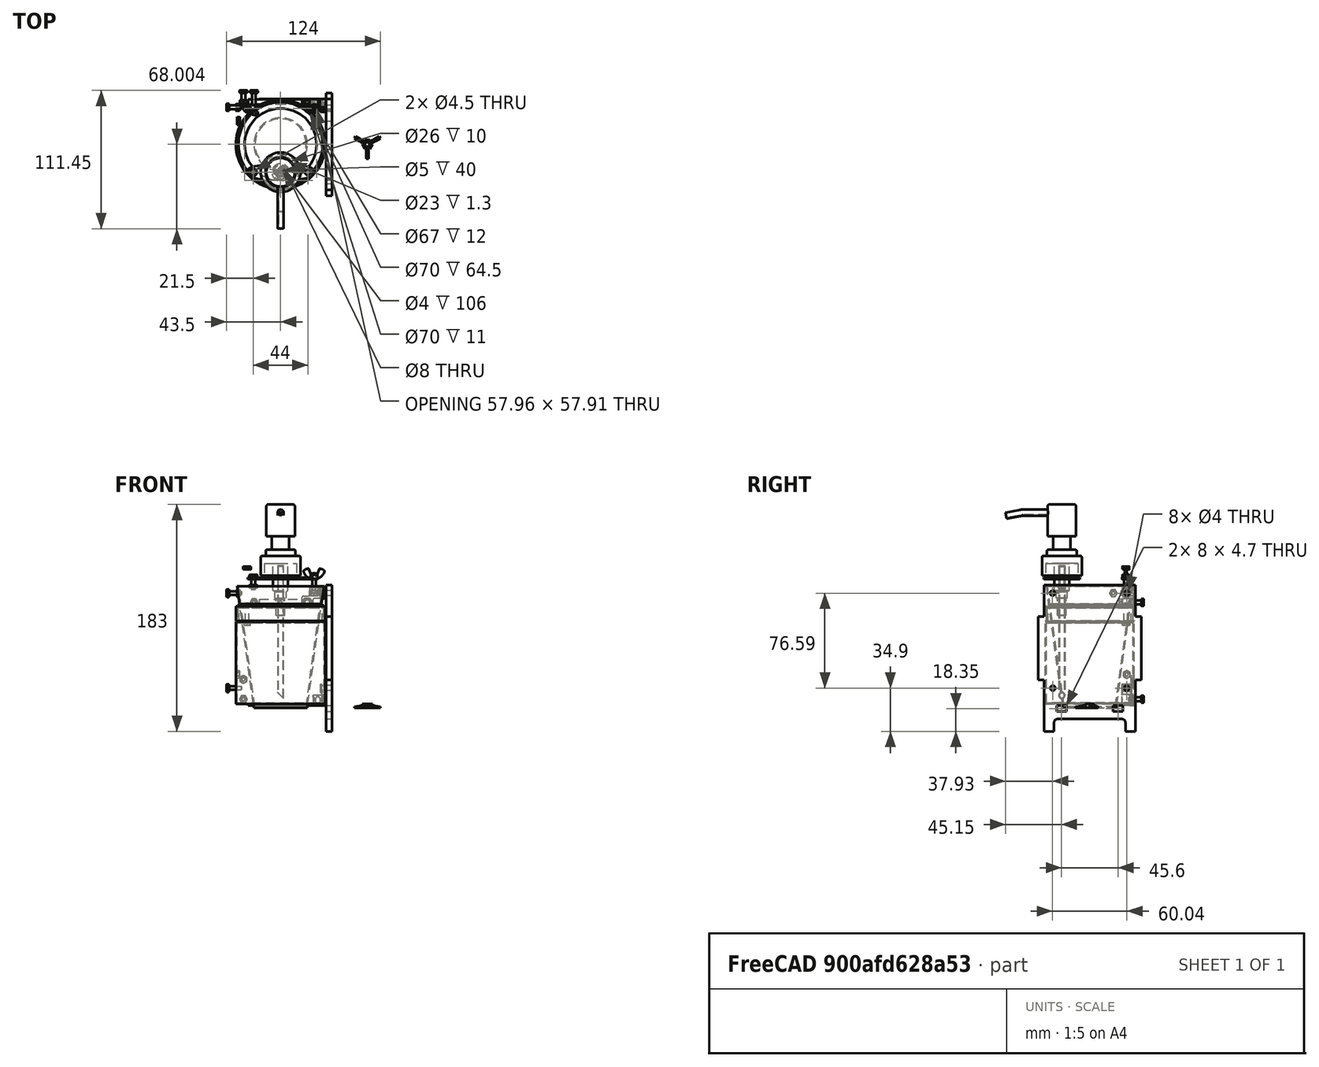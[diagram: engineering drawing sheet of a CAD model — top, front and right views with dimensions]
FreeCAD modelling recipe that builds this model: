
FCSTD DOCUMENT  (FreeCAD 0.20R29410 (Git))
Label: OrcuDispenser_78_realease_1_0
License: All rights reserved
LicenseURL: http://en.wikipedia.org/wiki/All_rights_reserved
objects: Sketcher::SketchObject×45, PartDesign::Body×36, PartDesign::Pad×23, PartDesign::FeatureBase×19, PartDesign::Pocket×16, Part::FeaturePython×14, PartDesign::Fillet×11, App::DocumentObjectGroup×10, Part::Part2DObjectPython×6, PartDesign::Revolution×4, PartDesign::Mirrored×4, Mesh::Feature×4, Part::Mirroring×2, Spreadsheet::Sheet×1, PartDesign::PolarPattern×1, PartDesign::AdditivePipe×1, PartDesign::Chamfer×1
note: 239 computed .brp shape members not serialized (recipe doc carries the construction recipe); baked Part::Feature solids carry a one-line shape summary decoded from their .brp

FEATURE [Sketcher::SketchObject] Sketch006
  FullyConstrained = true
  MapMode = 5
  Placement = pos=(0,0,0) rot=(1,0,0;1.5708rad)
  Support = -> [XZ_Plane004]
  sketch-geometry (6):
    g0: LineSegment StartX=0 StartY=0 StartZ=0 EndX=-21.5 EndY=0 EndZ=0
    g1: LineSegment StartX=-21.5 StartY=0 StartZ=0 EndX=-35 EndY=98 EndZ=0
    g2: LineSegment StartX=-20.6378 StartY=1 StartZ=0 EndX=0 EndY=1 EndZ=0
    g3: LineSegment StartX=0 StartY=1 StartZ=0 EndX=0 EndY=0 EndZ=0
    g4: LineSegment StartX=-20.6378 StartY=1 StartZ=0 EndX=-34 EndY=98 EndZ=0
    g5: LineSegment StartX=-34 StartY=98 StartZ=0 EndX=-35 EndY=98 EndZ=0
  constraints (17):
    c: Coincident(g-1,g0)
    c: PointOnObject(g0,g-1)
    c: Coincident(g0,g1)
    c: PointOnObject(g2,g-2)
    c: Horizontal(g2)
    c: Coincident(g2,g3)
    c: Coincident(g3,g0)
    c: DistanceX(g0,g0) = 21.5
    c: DistanceX(g1,g-1) = 35
    c: DistanceY(g-1,g1) = 98
    c: Coincident(g2,g4)
    c: Coincident(g4,g5)
    c: Coincident(g5,g1)
    c: Horizontal(g5)
    c: Parallel(g4,g1)
    c: DistanceX(g5,g5) = 1
    c: Equal(g3,g5)
FEATURE [PartDesign::Revolution] Revolution002
  Angle = 360
  Axis = (0,-2e-16,1)
  Base = (0,0,0)
  Placement = pos=(0,0,0) rot=(1,0,0;1.5708rad)
  Profile = -> Sketch006
  ReferenceAxis = -> Sketch006 [V_Axis]
FEATURE [PartDesign::Body] Body004  label="Cup (0,2 L)"
  Group = -> [Sketch006,Revolution002]
  Origin = -> Origin004
  Tip = -> Revolution002
FEATURE [Spreadsheet::Sheet] Spreadsheet  label="Parameters"
  cells = A2=Dispenser parameters; A3=123; B3= = Input cells (double-click and modify); A4=123; B4= = Output cells (value ist calculated, do not modify!); A6=Dispenser size; E6=Laser cutting; A7=PlateThickness; B7(PlateThickness)==4.7mm; E7=LCdistance; F7(LCdistance)==4mm; A8=Height; B8(Height)==102mm; A9=Length; B9(Length)==83mm; A10=Width; B10(Width)==83mm; A12=Element dimensions; A13=JointLength; B13(JointLength)==B8 / 2; C13= = Height / 2; A14=Tenon; B14(Tenon)==8mm; A15=LegHeight; B15(LegHeight)==10mm; A16=LegWidth; B16(LegWidth)==8mm; A17=LegRadius; B17(LegRadius)==3mm; A18=TenonDistance; B18(TenonDistance)==10mm; A19=TenonHeight; B19(TenonHeight)==6mm
FEATURE [Sketcher::SketchObject] Sketch012
  FullyConstrained = true
  MapMode = 5
  Support = -> [XY_Plane008]
  expr: Constraints[103] = <<Parameters>>.Width
  expr: Constraints[104] = <<Parameters>>.Length
  expr: Constraints[105] = <<Parameters>>.Width / 2 - <<Parameters>>.PlateThickness - <<Parameters>>.TenonDistance
  expr: Constraints[106] = <<Parameters>>.Length / 2 - <<Parameters>>.PlateThickness - <<Parameters>>.TenonDistance
  expr: Constraints[107] = <<Parameters>>.Width / 2 - <<Parameters>>.PlateThickness - <<Parameters>>.TenonDistance - <<Parameters>>.Tenon
  expr: Constraints[108] = <<Parameters>>.Length / 2 - <<Parameters>>.PlateThickness - <<Parameters>>.TenonDistance - <<Parameters>>.Tenon
  expr: Constraints[88] = <<Parameters>>.Length / 2 - <<Parameters>>.PlateThickness
  expr: Constraints[89] = <<Parameters>>.Width / 2 - <<Parameters>>.PlateThickness
  expr: Constraints[93] = <<Parameters>>.Length / 2 - <<Parameters>>.PlateThickness
  expr: Constraints[94] = <<Parameters>>.Width / 2 - <<Parameters>>.PlateThickness
  sketch-geometry (40):
    g0: LineSegment StartX=-41.5 StartY=41.5 StartZ=0 EndX=41.5 EndY=41.5 EndZ=0
    g1: LineSegment StartX=41.5 StartY=41.5 StartZ=0 EndX=41.5 EndY=-41.5 EndZ=0
    g2: LineSegment StartX=41.5 StartY=-41.5 StartZ=0 EndX=-41.5 EndY=-41.5 EndZ=0
    g3: LineSegment StartX=-41.5 StartY=-41.5 StartZ=0 EndX=-41.5 EndY=41.5 EndZ=0
    g4: LineSegment StartX=-36.8 StartY=-36.8 StartZ=0 EndX=-26.8 EndY=-36.8 EndZ=0
    g5: LineSegment StartX=-26.8 StartY=-36.8 StartZ=0 EndX=-26.8 EndY=-41.5 EndZ=0
    g6: LineSegment StartX=-26.8 StartY=-41.5 StartZ=0 EndX=-18.8 EndY=-41.5 EndZ=0
    g7: LineSegment StartX=-18.8 StartY=-41.5 StartZ=0 EndX=-18.8 EndY=-36.8 EndZ=0
    g8: LineSegment StartX=-18.8 StartY=-36.8 StartZ=0 EndX=18.8 EndY=-36.8 EndZ=0
    g9: LineSegment StartX=18.8 StartY=-36.8 StartZ=0 EndX=18.8 EndY=-41.5 EndZ=0
    g10: LineSegment StartX=18.8 StartY=-41.5 StartZ=0 EndX=26.8 EndY=-41.5 EndZ=0
    g11: LineSegment StartX=26.8 StartY=-41.5 StartZ=0 EndX=26.8 EndY=-36.8 EndZ=0
    g12: LineSegment StartX=26.8 StartY=-36.8 StartZ=0 EndX=36.8 EndY=-36.8 EndZ=0
    g13: LineSegment StartX=36.8 StartY=-36.8 StartZ=0 EndX=36.8 EndY=-26.8 EndZ=0
    g14: LineSegment StartX=36.8 StartY=-26.8 StartZ=0 EndX=41.5 EndY=-26.8 EndZ=0
    g15: LineSegment StartX=41.5 StartY=-26.8 StartZ=0 EndX=41.5 EndY=-18.8 EndZ=0
    g16: LineSegment StartX=41.5 StartY=-18.8 StartZ=0 EndX=36.8 EndY=-18.8 EndZ=0
    g17: LineSegment StartX=36.8 StartY=-18.8 StartZ=0 EndX=36.8 EndY=18.8 EndZ=0
    g18: LineSegment StartX=36.8 StartY=18.8 StartZ=0 EndX=41.5 EndY=18.8 EndZ=0
    g19: LineSegment StartX=41.5 StartY=18.8 StartZ=0 EndX=41.5 EndY=26.8 EndZ=0
    g20: LineSegment StartX=41.5 StartY=26.8 StartZ=0 EndX=36.8 EndY=26.8 EndZ=0
    g21: LineSegment StartX=36.8 StartY=26.8 StartZ=0 EndX=36.8 EndY=36.8 EndZ=0
    g22: LineSegment StartX=36.8 StartY=36.8 StartZ=0 EndX=26.8 EndY=36.8 EndZ=0
    g23: LineSegment StartX=26.8 StartY=36.8 StartZ=0 EndX=26.8 EndY=41.5 EndZ=0
    g24: LineSegment StartX=26.8 StartY=41.5 StartZ=0 EndX=18.8 EndY=41.5 EndZ=0
    g25: LineSegment StartX=18.8 StartY=41.5 StartZ=0 EndX=18.8 EndY=36.8 EndZ=0
    g26: LineSegment StartX=18.8 StartY=36.8 StartZ=0 EndX=-18.8 EndY=36.8 EndZ=0
    g27: LineSegment StartX=-18.8 StartY=36.8 StartZ=0 EndX=-18.8 EndY=41.5 EndZ=0
    g28: LineSegment StartX=-18.8 StartY=41.5 StartZ=0 EndX=-26.8 EndY=41.5 EndZ=0
    g29: LineSegment StartX=-26.8 StartY=41.5 StartZ=0 EndX=-26.8 EndY=36.8 EndZ=0
    g30: LineSegment StartX=-26.8 StartY=36.8 StartZ=0 EndX=-36.8 EndY=36.8 EndZ=0
    g31: LineSegment StartX=-36.8 StartY=36.8 StartZ=0 EndX=-36.8 EndY=26.8 EndZ=0
    g32: LineSegment StartX=-36.8 StartY=26.8 StartZ=0 EndX=-41.5 EndY=26.8 EndZ=0
    g33: LineSegment StartX=-41.5 StartY=26.8 StartZ=0 EndX=-41.5 EndY=18.8 EndZ=0
    g34: LineSegment StartX=-41.5 StartY=18.8 StartZ=0 EndX=-36.8 EndY=18.8 EndZ=0
    g35: LineSegment StartX=-36.8 StartY=18.8 StartZ=0 EndX=-36.8 EndY=-18.8 EndZ=0
    g36: LineSegment StartX=-36.8 StartY=-18.8 StartZ=0 EndX=-41.5 EndY=-18.8 EndZ=0
    g37: LineSegment StartX=-41.5 StartY=-18.8 StartZ=0 EndX=-41.5 EndY=-26.8 EndZ=0
    g38: LineSegment StartX=-41.5 StartY=-26.8 StartZ=0 EndX=-36.8 EndY=-26.8 EndZ=0
    g39: LineSegment StartX=-36.8 StartY=-26.8 StartZ=0 EndX=-36.8 EndY=-36.8 EndZ=0
  constraints (109):
    c: Coincident(g0,g1)
    c: Coincident(g1,g2)
    c: Coincident(g2,g3)
    c: Coincident(g3,g0)
    c: Horizontal(g0)
    c: Vertical(g1)
    c: Horizontal(g4)
    c: Coincident(g4,g5)
    c: PointOnObject(g5,g2)
    c: Vertical(g5)
    c: Coincident(g5,g6)
    c: PointOnObject(g6,g2)
    c: Coincident(g6,g7)
    c: Vertical(g7)
    c: Coincident(g7,g8)
    c: Coincident(g8,g9)
    c: PointOnObject(g9,g2)
    c: Vertical(g9)
    c: Coincident(g9,g10)
    c: PointOnObject(g10,g2)
    c: Coincident(g10,g11)
    c: Vertical(g11)
    c: Coincident(g11,g12)
    c: Horizontal(g12)
    c: Coincident(g12,g13)
    c: Vertical(g13)
    c: Coincident(g13,g14)
    c: PointOnObject(g14,g1)
    c: Coincident(g14,g15)
    c: PointOnObject(g15,g1)
    c: Coincident(g15,g16)
    c: Horizontal(g16)
    c: Coincident(g16,g17)
    c: Vertical(g17)
    c: Coincident(g17,g18)
    c: PointOnObject(g18,g1)
    c: Horizontal(g18)
    c: Coincident(g18,g19)
    c: PointOnObject(g19,g1)
    c: Coincident(g19,g20)
    c: Horizontal(g20)
    c: Coincident(g20,g21)
    c: Vertical(g21)
    c: Coincident(g21,g22)
    c: Horizontal(g22)
    c: Coincident(g22,g23)
    c: PointOnObject(g23,g0)
    c: Vertical(g23)
    c: Coincident(g23,g24)
    c: PointOnObject(g24,g0)
    c: Coincident(g24,g25)
    c: Vertical(g25)
    c: Coincident(g25,g26)
    c: Horizontal(g26)
    c: Coincident(g26,g27)
    c: PointOnObject(g27,g0)
    c: Vertical(g27)
    c: Coincident(g27,g28)
    c: PointOnObject(g28,g0)
    c: Coincident(g28,g29)
    c: Vertical(g29)
    c: Coincident(g29,g30)
    c: Coincident(g30,g31)
    c: Vertical(g31)
    c: Coincident(g31,g32)
    c: PointOnObject(g32,g3)
    c: Horizontal(g32)
    c: Coincident(g32,g33)
    c: PointOnObject(g33,g3)
    c: Coincident(g33,g34)
    c: Horizontal(g34)
    c: Coincident(g34,g35)
    c: Coincident(g35,g36)
    c: Horizontal(g36)
    c: Coincident(g36,g37)
    c: PointOnObject(g37,g3)
    c: Coincident(g37,g38)
    c: Horizontal(g38)
    c: Coincident(g38,g39)
    c: Coincident(g39,g4)
    c: Vertical(g39)
    c: Horizontal(g14)
    c: Equal(g10,g6)
    c: Equal(g37,g33)
    c: Equal(g28,g24)
    c: Equal(g24,g19)
    c: Symmetric(g1,g2,g-2)
    c: Symmetric(g2,g0,g-1)
    c: DistanceY(g7,g-1) = 36.8
    c: DistanceX(g38,g-1) = 36.8
    c: Symmetric(g29,g4,g-1)
    c: Symmetric(g7,g26,g-1)
    c: Symmetric(g11,g22,g-1)
    c: DistanceY(g4,g-1) = 36.8
    c: DistanceX(g35,g-1) = 36.8
    c: Symmetric(g36,g33,g-1)
    c: Symmetric(g38,g13,g-2)
    c: Symmetric(g35,g16,g-2)
    c: Symmetric(g31,g20,g-2)
    c: Symmetric(g4,g30,g-1)
    c: Vertical(g35)
    c: Horizontal(g8)
    c: Symmetric(g11,g4,g-2)
    c: DistanceX(g2,g2) = 83
    c: DistanceY(g3,g3) = 83
    c: DistanceX(g4,g-1) = 26.8
    c: DistanceY(g38,g-1) = 26.8
    c: DistanceX(g6,g-1) = 18.8
    c: DistanceY(g36,g-1) = 18.8
FEATURE [PartDesign::Pad] Pad008
  AlongSketchNormal = false
  Direction = (0,0,1)
  Length = 4.7
  Length2 = 100
  Profile = -> Sketch012
  Reversed = true
  Type = 0
  expr: Length = <<Parameters>>.PlateThickness
FEATURE [PartDesign::Body] Body008  label="Bottom"
  Group = -> [Sketch012,Pad008]
  Origin = -> Origin008
  Placement = pos=(0,0,1.7) rot=(0,0,1;0rad)
  Tip = -> Pad008
  expr: .Placement.Base.z = <<Parameters>>.PlateThickness - 3mm - (<<Parameters>>.Height - 102mm) / 2
FEATURE [Sketcher::SketchObject] Sketch013
  FullyConstrained = true
  MapMode = 5
  Placement = pos=(0,0,0) rot=(1,0,0;1.5708rad)
  Support = -> [XZ_Plane009]
  expr: Constraints[32] = <<Parameters>>.JointLength
  expr: Constraints[35] = <<Parameters>>.PlateThickness
  expr: Constraints[50] = <<Parameters>>.LegWidth
  expr: Constraints[51] = <<Parameters>>.LegHeight
  expr: Constraints[53] = <<Parameters>>.LegHeight + <<Parameters>>.TenonHeight
  expr: Constraints[62] = <<Parameters>>.Tenon
  expr: Constraints[63] = <<Parameters>>.PlateThickness
  expr: Constraints[64] = <<Parameters>>.TenonDistance + <<Parameters>>.PlateThickness
  expr: Constraints[8] = <<Parameters>>.Width
  expr: Constraints[9] = <<Parameters>>.Height
  sketch-geometry (30):
    g0: LineSegment StartX=-41.5 StartY=51 StartZ=0 EndX=41.5 EndY=51 EndZ=0
    g1: LineSegment StartX=41.5 StartY=51 StartZ=0 EndX=41.5 EndY=-51 EndZ=0
    g2: LineSegment StartX=41.5 StartY=-51 StartZ=0 EndX=-41.5 EndY=-51 EndZ=0
    g3: LineSegment StartX=-41.5 StartY=-51 StartZ=0 EndX=-41.5 EndY=51 EndZ=0
    g4: LineSegment StartX=-41.5 StartY=-51 StartZ=0 EndX=-41.5 EndY=-25.5 EndZ=0
    g5: LineSegment StartX=-41.5 StartY=-25.5 StartZ=0 EndX=-36.8 EndY=-25.5 EndZ=0
    g6: LineSegment StartX=-36.8 StartY=-25.5 StartZ=0 EndX=-36.8 EndY=25.5 EndZ=0
    g7: LineSegment StartX=-36.8 StartY=25.5 StartZ=0 EndX=-41.5 EndY=25.5 EndZ=0
    g8: LineSegment StartX=-41.5 StartY=25.5 StartZ=0 EndX=-41.5 EndY=51 EndZ=0
    g9: LineSegment StartX=-41.5 StartY=51 StartZ=0 EndX=41.5 EndY=51 EndZ=0
    g10: LineSegment StartX=41.5 StartY=51 StartZ=0 EndX=41.5 EndY=25.5 EndZ=0
    g11: LineSegment StartX=41.5 StartY=25.5 StartZ=0 EndX=36.8 EndY=25.5 EndZ=0
    g12: LineSegment StartX=36.8 StartY=25.5 StartZ=0 EndX=36.8 EndY=-25.5 EndZ=0
    g13: LineSegment StartX=36.8 StartY=-25.5 StartZ=0 EndX=41.5 EndY=-25.5 EndZ=0
    g14: LineSegment StartX=41.5 StartY=-25.5 StartZ=0 EndX=41.5 EndY=-51 EndZ=0
    g15: LineSegment StartX=-41.5 StartY=-51 StartZ=0 EndX=-41.5 EndY=-67 EndZ=0
    g16: LineSegment StartX=-41.5 StartY=-67 StartZ=0 EndX=-33.5 EndY=-67 EndZ=0
    g17: LineSegment StartX=-33.5 StartY=-67 StartZ=0 EndX=-33.5 EndY=-57 EndZ=0
    g18: LineSegment StartX=-33.5 StartY=-57 StartZ=0 EndX=33.5 EndY=-57 EndZ=0
    g19: LineSegment StartX=33.5 StartY=-57 StartZ=0 EndX=33.5 EndY=-67 EndZ=0
    g20: LineSegment StartX=33.5 StartY=-67 StartZ=0 EndX=41.5 EndY=-67 EndZ=0
    g21: LineSegment StartX=41.5 StartY=-67 StartZ=0 EndX=41.5 EndY=-51 EndZ=0
    g22: LineSegment StartX=-26.8 StartY=-46.3 StartZ=0 EndX=-18.8 EndY=-46.3 EndZ=0
    g23: LineSegment StartX=-18.8 StartY=-46.3 StartZ=0 EndX=-18.8 EndY=-51 EndZ=0
    g24: LineSegment StartX=-18.8 StartY=-51 StartZ=0 EndX=-26.8 EndY=-51 EndZ=0
    g25: LineSegment StartX=-26.8 StartY=-51 StartZ=0 EndX=-26.8 EndY=-46.3 EndZ=0
    g26: LineSegment StartX=18.8 StartY=-46.3 StartZ=0 EndX=26.8 EndY=-46.3 EndZ=0
    g27: LineSegment StartX=26.8 StartY=-46.3 StartZ=0 EndX=26.8 EndY=-51 EndZ=0
    g28: LineSegment StartX=26.8 StartY=-51 StartZ=0 EndX=18.8 EndY=-51 EndZ=0
    g29: LineSegment StartX=18.8 StartY=-51 StartZ=0 EndX=18.8 EndY=-46.3 EndZ=0
  constraints (78):
    c: Coincident(g0,g1)
    c: Coincident(g1,g2)
    c: Coincident(g2,g3)
    c: Coincident(g3,g0)
    c: Horizontal(g0)
    c: Vertical(g1)
    c: Symmetric(g2,g1,g-2)
    c: Symmetric(g2,g0,g-1)
    c: DistanceX(g2,g2) = 83
    c: DistanceY(g3,g3) = 102
    c: Coincident(g2,g4)
    c: PointOnObject(g4,g3)
    c: Coincident(g4,g5)
    c: Horizontal(g5)
    c: Coincident(g5,g6)
    c: Vertical(g6)
    c: Coincident(g6,g7)
    c: Horizontal(g7)
    c: Coincident(g7,g8)
    c: Coincident(g8,g0)
    c: Coincident(g8,g9)
    c: Coincident(g9,g0)
    c: Coincident(g9,g10)
    c: PointOnObject(g10,g1)
    c: Coincident(g10,g11)
    c: Horizontal(g11)
    c: Coincident(g11,g12)
    c: Vertical(g12)
    c: Coincident(g12,g13)
    c: Horizontal(g13)
    c: Coincident(g13,g14)
    c: Coincident(g14,g1)
    c: DistanceY(g6,g6) = 51
    c: Symmetric(g7,g4,g-1)
    c: Symmetric(g10,g13,g-1)
    c: DistanceX(g7,g7) = 4.7
    c: Coincident(g4,g15)
    c: Vertical(g15)
    c: Coincident(g15,g16)
    c: Horizontal(g16)
    c: Coincident(g16,g17)
    c: Vertical(g17)
    c: Coincident(g17,g18)
    c: Coincident(g18,g19)
    c: Vertical(g19)
    c: Coincident(g19,g20)
    c: Horizontal(g20)
    c: Coincident(g20,g21)
    c: Coincident(g21,g14)
    c: Vertical(g21)
    c: DistanceX(g16,g16) = 8
    c: DistanceY(g17,g17) = 10
    c: Equal(g19,g17)
    c: DistanceY(g15,g15) = 16
    c: Coincident(g22,g23)
    c: Coincident(g23,g24)
    c: Coincident(g24,g25)
    c: Coincident(g25,g22)
    c: Horizontal(g22)
    c: Horizontal(g24)
    c: Vertical(g23)
    c: Vertical(g25)
    c: DistanceX(g24,g24) = 8
    c: DistanceY(g25,g25) = 4.7
    c: DistanceX(g4,g24) = 14.7
    c: PointOnObject(g24,g2)
    c: Coincident(g26,g27)
    c: Coincident(g27,g28)
    c: Coincident(g28,g29)
    c: Coincident(g29,g26)
    c: Horizontal(g26)
    c: Horizontal(g28)
    c: Vertical(g27)
    c: Vertical(g29)
    c: Symmetric(g28,g23,g-2)
    c: Symmetric(g26,g22,g-2)
    c: Symmetric(g18,g17,g-2)
    c: Symmetric(g11,g6,g-2)
FEATURE [PartDesign::Pad] Pad009
  AlongSketchNormal = false
  Direction = (0,-1,-2e-16)
  Length = 4.7
  Length2 = 100
  Placement = pos=(0,0,0) rot=(1,0,0;1.5708rad)
  Profile = -> Sketch013
  Type = 0
  expr: Length = <<Parameters>>.PlateThickness
FEATURE [Sketcher::SketchObject] Sketch014
  FullyConstrained = true
  MapMode = 5
  Placement = pos=(0,0,0) rot=(1,0,0;1.5708rad)
  Support = -> [XZ_Plane010]
  expr: Constraints[32] = <<Parameters>>.JointLength
  expr: Constraints[35] = <<Parameters>>.PlateThickness
  expr: Constraints[50] = <<Parameters>>.LegWidth
  expr: Constraints[51] = <<Parameters>>.LegHeight
  expr: Constraints[53] = <<Parameters>>.LegHeight + <<Parameters>>.TenonHeight
  expr: Constraints[62] = <<Parameters>>.Tenon
  expr: Constraints[63] = <<Parameters>>.PlateThickness
  expr: Constraints[64] = <<Parameters>>.TenonDistance + <<Parameters>>.PlateThickness
  expr: Constraints[8] = <<Parameters>>.Width
  expr: Constraints[9] = <<Parameters>>.Height
  sketch-geometry (30):
    g0: LineSegment StartX=-41.5 StartY=51 StartZ=0 EndX=41.5 EndY=51 EndZ=0
    g1: LineSegment StartX=41.5 StartY=51 StartZ=0 EndX=41.5 EndY=-51 EndZ=0
    g2: LineSegment StartX=41.5 StartY=-51 StartZ=0 EndX=-41.5 EndY=-51 EndZ=0
    g3: LineSegment StartX=-41.5 StartY=-51 StartZ=0 EndX=-41.5 EndY=51 EndZ=0
    g4: LineSegment StartX=-41.5 StartY=-51 StartZ=0 EndX=-41.5 EndY=-25.5 EndZ=0
    g5: LineSegment StartX=-41.5 StartY=-25.5 StartZ=0 EndX=-36.8 EndY=-25.5 EndZ=0
    g6: LineSegment StartX=-36.8 StartY=-25.5 StartZ=0 EndX=-36.8 EndY=25.5 EndZ=0
    g7: LineSegment StartX=-36.8 StartY=25.5 StartZ=0 EndX=-41.5 EndY=25.5 EndZ=0
    g8: LineSegment StartX=-41.5 StartY=25.5 StartZ=0 EndX=-41.5 EndY=51 EndZ=0
    g9: LineSegment StartX=-41.5 StartY=51 StartZ=0 EndX=41.5 EndY=51 EndZ=0
    g10: LineSegment StartX=41.5 StartY=51 StartZ=0 EndX=41.5 EndY=25.5 EndZ=0
    g11: LineSegment StartX=41.5 StartY=25.5 StartZ=0 EndX=36.8 EndY=25.5 EndZ=0
    g12: LineSegment StartX=36.8 StartY=25.5 StartZ=0 EndX=36.8 EndY=-25.5 EndZ=0
    g13: LineSegment StartX=36.8 StartY=-25.5 StartZ=0 EndX=41.5 EndY=-25.5 EndZ=0
    g14: LineSegment StartX=41.5 StartY=-25.5 StartZ=0 EndX=41.5 EndY=-51 EndZ=0
    g15: LineSegment StartX=-41.5 StartY=-51 StartZ=0 EndX=-41.5 EndY=-67 EndZ=0
    g16: LineSegment StartX=-41.5 StartY=-67 StartZ=0 EndX=-33.5 EndY=-67 EndZ=0
    g17: LineSegment StartX=-33.5 StartY=-67 StartZ=0 EndX=-33.5 EndY=-57 EndZ=0
    g18: LineSegment StartX=-33.5 StartY=-57 StartZ=0 EndX=33.5 EndY=-57 EndZ=0
    g19: LineSegment StartX=33.5 StartY=-57 StartZ=0 EndX=33.5 EndY=-67 EndZ=0
    g20: LineSegment StartX=33.5 StartY=-67 StartZ=0 EndX=41.5 EndY=-67 EndZ=0
    g21: LineSegment StartX=41.5 StartY=-67 StartZ=0 EndX=41.5 EndY=-51 EndZ=0
    g22: LineSegment StartX=-26.8 StartY=-46.3 StartZ=0 EndX=-18.8 EndY=-46.3 EndZ=0
    g23: LineSegment StartX=-18.8 StartY=-46.3 StartZ=0 EndX=-18.8 EndY=-51 EndZ=0
    g24: LineSegment StartX=-18.8 StartY=-51 StartZ=0 EndX=-26.8 EndY=-51 EndZ=0
    g25: LineSegment StartX=-26.8 StartY=-51 StartZ=0 EndX=-26.8 EndY=-46.3 EndZ=0
    g26: LineSegment StartX=18.8 StartY=-46.3 StartZ=0 EndX=26.8 EndY=-46.3 EndZ=0
    g27: LineSegment StartX=26.8 StartY=-46.3 StartZ=0 EndX=26.8 EndY=-51 EndZ=0
    g28: LineSegment StartX=26.8 StartY=-51 StartZ=0 EndX=18.8 EndY=-51 EndZ=0
    g29: LineSegment StartX=18.8 StartY=-51 StartZ=0 EndX=18.8 EndY=-46.3 EndZ=0
  constraints (78):
    c: Coincident(g0,g1)
    c: Coincident(g1,g2)
    c: Coincident(g2,g3)
    c: Coincident(g3,g0)
    c: Horizontal(g0)
    c: Vertical(g1)
    c: Symmetric(g2,g1,g-2)
    c: Symmetric(g2,g0,g-1)
    c: DistanceX(g2,g2) = 83
    c: DistanceY(g3,g3) = 102
    c: Coincident(g2,g4)
    c: PointOnObject(g4,g3)
    c: Coincident(g4,g5)
    c: Horizontal(g5)
    c: Coincident(g5,g6)
    c: Vertical(g6)
    c: Coincident(g6,g7)
    c: Horizontal(g7)
    c: Coincident(g7,g8)
    c: Coincident(g8,g0)
    c: Coincident(g8,g9)
    c: Coincident(g9,g0)
    c: Coincident(g9,g10)
    c: PointOnObject(g10,g1)
    c: Coincident(g10,g11)
    c: Horizontal(g11)
    c: Coincident(g11,g12)
    c: Vertical(g12)
    c: Coincident(g12,g13)
    c: Horizontal(g13)
    c: Coincident(g13,g14)
    c: Coincident(g14,g1)
    c: DistanceY(g6,g6) = 51
    c: Symmetric(g7,g4,g-1)
    c: Symmetric(g10,g13,g-1)
    c: DistanceX(g7,g7) = 4.7
    c: Coincident(g4,g15)
    c: Vertical(g15)
    c: Coincident(g15,g16)
    c: Horizontal(g16)
    c: Coincident(g16,g17)
    c: Vertical(g17)
    c: Coincident(g17,g18)
    c: Coincident(g18,g19)
    c: Vertical(g19)
    c: Coincident(g19,g20)
    c: Horizontal(g20)
    c: Coincident(g20,g21)
    c: Coincident(g21,g14)
    c: Vertical(g21)
    c: DistanceX(g16,g16) = 8
    c: DistanceY(g17,g17) = 10
    c: Equal(g19,g17)
    c: DistanceY(g15,g15) = 16
    c: Coincident(g22,g23)
    c: Coincident(g23,g24)
    c: Coincident(g24,g25)
    c: Coincident(g25,g22)
    c: Horizontal(g22)
    c: Horizontal(g24)
    c: Vertical(g23)
    c: Vertical(g25)
    c: DistanceX(g24,g24) = 8
    c: DistanceY(g25,g25) = 4.7
    c: DistanceX(g4,g24) = 14.7
    c: PointOnObject(g24,g2)
    c: Coincident(g26,g27)
    c: Coincident(g27,g28)
    c: Coincident(g28,g29)
    c: Coincident(g29,g26)
    c: Horizontal(g26)
    c: Horizontal(g28)
    c: Vertical(g27)
    c: Vertical(g29)
    c: Symmetric(g28,g23,g-2)
    c: Symmetric(g26,g22,g-2)
    c: Symmetric(g18,g17,g-2)
    c: Symmetric(g11,g6,g-2)
FEATURE [PartDesign::Pad] Pad010
  AlongSketchNormal = false
  Direction = (0,-1,-2e-16)
  Length = 4.7
  Length2 = 100
  Placement = pos=(0,0,0) rot=(1,0,0;1.5708rad)
  Profile = -> Sketch014
  ReferenceAxis = -> Sketch014 [N_Axis]
  Type = 0
  expr: Length = <<Parameters>>.PlateThickness
FEATURE [Sketcher::SketchObject] Sketch015
  FullyConstrained = true
  MapMode = 5
  Placement = pos=(0,0,0) rot=(1,0,0;1.5708rad)
  Support = -> [XZ_Plane011]
  expr: Constraints[10] = <<Parameters>>.JointLength
  expr: Constraints[16] = <<Parameters>>.LegHeight
  expr: Constraints[26] = <<Parameters>>.Tenon
  expr: Constraints[27] = <<Parameters>>.PlateThickness
  expr: Constraints[28] = <<Parameters>>.TenonDistance + <<Parameters>>.PlateThickness
  expr: Constraints[73] = <<Parameters>>.PlateThickness
  expr: Constraints[75] = <<Parameters>>.LegWidth
  expr: Constraints[76] = <<Parameters>>.LegHeight + <<Parameters>>.TenonHeight
  expr: Constraints[8] = <<Parameters>>.Length
  expr: Constraints[9] = <<Parameters>>.Height
  sketch-geometry (30):
    g0: LineSegment StartX=-41.5 StartY=51 StartZ=0 EndX=41.5 EndY=51 EndZ=0
    g1: LineSegment StartX=41.5 StartY=51 StartZ=0 EndX=41.5 EndY=-51 EndZ=0
    g2: LineSegment StartX=41.5 StartY=-51 StartZ=0 EndX=-41.5 EndY=-51 EndZ=0
    g3: LineSegment StartX=-41.5 StartY=-51 StartZ=0 EndX=-41.5 EndY=51 EndZ=0
    g4: LineSegment StartX=-41.5 StartY=-25.5 StartZ=0 EndX=-41.5 EndY=25.5 EndZ=0
    g5: LineSegment StartX=41.5 StartY=25.5 StartZ=0 EndX=41.5 EndY=-25.5 EndZ=0
    g6: LineSegment StartX=-28.8 StartY=-67 StartZ=0 EndX=-28.8 EndY=-57 EndZ=0
    g7: LineSegment StartX=-28.8 StartY=-57 StartZ=0 EndX=28.8 EndY=-57 EndZ=0
    g8: LineSegment StartX=28.8 StartY=-57 StartZ=0 EndX=28.8 EndY=-67 EndZ=0
    g9: LineSegment StartX=-26.8 StartY=-46.3 StartZ=0 EndX=-18.8 EndY=-46.3 EndZ=0
    g10: LineSegment StartX=-18.8 StartY=-46.3 StartZ=0 EndX=-18.8 EndY=-51 EndZ=0
    g11: LineSegment StartX=-18.8 StartY=-51 StartZ=0 EndX=-26.8 EndY=-51 EndZ=0
    g12: LineSegment StartX=-26.8 StartY=-51 StartZ=0 EndX=-26.8 EndY=-46.3 EndZ=0
    g13: LineSegment StartX=18.8 StartY=-46.3 StartZ=0 EndX=26.8 EndY=-46.3 EndZ=0
    g14: LineSegment StartX=26.8 StartY=-46.3 StartZ=0 EndX=26.8 EndY=-51 EndZ=0
    g15: LineSegment StartX=26.8 StartY=-51 StartZ=0 EndX=18.8 EndY=-51 EndZ=0
    g16: LineSegment StartX=18.8 StartY=-51 StartZ=0 EndX=18.8 EndY=-46.3 EndZ=0
    g17: LineSegment StartX=-41.5 StartY=-25.5 StartZ=0 EndX=-36.8 EndY=-25.5 EndZ=0
    g18: LineSegment StartX=-36.8 StartY=-67 StartZ=0 EndX=-28.8 EndY=-67 EndZ=0
    g19: LineSegment StartX=28.8 StartY=-67 StartZ=0 EndX=36.8 EndY=-67 EndZ=0
    g20: LineSegment StartX=-36.8 StartY=-25.5 StartZ=0 EndX=-36.8 EndY=-51 EndZ=0
    g21: LineSegment StartX=-36.8 StartY=-51 StartZ=0 EndX=-36.8 EndY=-67 EndZ=0
    g22: LineSegment StartX=36.8 StartY=-67 StartZ=0 EndX=36.8 EndY=-51 EndZ=0
    g23: LineSegment StartX=36.8 StartY=-51 StartZ=0 EndX=36.8 EndY=-25.5 EndZ=0
    g24: LineSegment StartX=36.8 StartY=-25.5 StartZ=0 EndX=41.5 EndY=-25.5 EndZ=0
    g25: LineSegment StartX=-41.5 StartY=25.5 StartZ=0 EndX=-36.8 EndY=25.5 EndZ=0
    g26: LineSegment StartX=-36.8 StartY=25.5 StartZ=0 EndX=-36.8 EndY=51 EndZ=0
    g27: LineSegment StartX=-36.8 StartY=51 StartZ=0 EndX=36.8 EndY=51 EndZ=0
    g28: LineSegment StartX=36.8 StartY=51 StartZ=0 EndX=36.8 EndY=25.5 EndZ=0
    g29: LineSegment StartX=36.8 StartY=25.5 StartZ=0 EndX=41.5 EndY=25.5 EndZ=0
  constraints (81):
    c: Coincident(g0,g1)
    c: Coincident(g1,g2)
    c: Coincident(g2,g3)
    c: Coincident(g3,g0)
    c: Horizontal(g0)
    c: Vertical(g1)
    c: Symmetric(g2,g1,g-2)
    c: Symmetric(g2,g0,g-1)
    c: DistanceX(g2,g2) = 83
    c: DistanceY(g3,g3) = 102
    c: DistanceY(g4,g4) = 51
    c: Equal(g5,g4)
    c: Vertical(g6)
    c: Coincident(g6,g7)
    c: Coincident(g7,g8)
    c: Vertical(g8)
    c: DistanceY(g6,g6) = 10
    c: Equal(g8,g6)
    c: Coincident(g9,g10)
    c: Coincident(g10,g11)
    c: Coincident(g11,g12)
    c: Coincident(g12,g9)
    c: Horizontal(g9)
    c: Horizontal(g11)
    c: Vertical(g10)
    c: Vertical(g12)
    c: DistanceX(g11,g11) = 8
    c: DistanceY(g12,g12) = 4.7
    c: DistanceX(g2,g11) = 14.7
    c: PointOnObject(g11,g2)
    c: Coincident(g13,g14)
    c: Coincident(g14,g15)
    c: Coincident(g15,g16)
    c: Coincident(g16,g13)
    c: Horizontal(g13)
    c: Horizontal(g15)
    c: Vertical(g14)
    c: Vertical(g16)
    c: Symmetric(g15,g10,g-2)
    c: Symmetric(g4,g4,g-1)
    c: PointOnObject(g4,g3)
    c: PointOnObject(g5,g1)
    c: Symmetric(g5,g5,g-1)
    c: Coincident(g4,g17)
    c: Horizontal(g17)
    c: Coincident(g18,g6)
    c: Horizontal(g18)
    c: Coincident(g8,g19)
    c: Horizontal(g19)
    c: Coincident(g17,g20)
    c: PointOnObject(g20,g2)
    c: Vertical(g20)
    c: Coincident(g20,g21)
    c: Coincident(g21,g18)
    c: Vertical(g21)
    c: Coincident(g19,g22)
    c: PointOnObject(g22,g2)
    c: Vertical(g22)
    c: Coincident(g22,g23)
    c: Vertical(g23)
    c: Coincident(g23,g24)
    c: Coincident(g24,g5)
    c: Coincident(g4,g25)
    c: Horizontal(g25)
    c: Coincident(g25,g26)
    c: PointOnObject(g26,g0)
    c: Vertical(g26)
    c: Coincident(g26,g27)
    c: PointOnObject(g27,g0)
    c: Coincident(g27,g28)
    c: Vertical(g28)
    c: Coincident(g28,g29)
    c: Coincident(g29,g5)
    c: DistanceX(g25,g25) = 4.7
    c: Equal(g17,g25)
    c: DistanceX(g18,g18) = 8
    c: DistanceY(g21,g21) = 16
    c: Symmetric(g9,g13,g-2)
    c: Symmetric(g7,g6,g-2)
    c: Symmetric(g28,g25,g-2)
    c: Symmetric(g17,g23,g-2)
FEATURE [PartDesign::Pad] Pad011
  AlongSketchNormal = false
  Direction = (0,-1,-2e-16)
  Length = 4.7
  Length2 = 100
  Placement = pos=(0,0,0) rot=(1,0,0;1.5708rad)
  Profile = -> Sketch015
  ReferenceAxis = -> Sketch015 [N_Axis]
  Type = 0
  expr: Length = <<Parameters>>.PlateThickness
FEATURE [Sketcher::SketchObject] Sketch016
  FullyConstrained = true
  MapMode = 5
  Support = -> [XY_Plane013]
  expr: Constraints[8] = <<Parameters>>.Width + 6mm
  expr: Constraints[9] = <<Parameters>>.Length + 6mm
  sketch-geometry (9):
    g0: LineSegment StartX=-44.5 StartY=44.5 StartZ=0 EndX=44.5 EndY=44.5 EndZ=0
    g1: LineSegment StartX=44.5 StartY=44.5 StartZ=0 EndX=44.5 EndY=-44.5 EndZ=0
    g2: LineSegment StartX=44.5 StartY=-44.5 StartZ=0 EndX=-44.5 EndY=-44.5 EndZ=0
    g3: LineSegment StartX=-44.5 StartY=-44.5 StartZ=0 EndX=-44.5 EndY=44.5 EndZ=0
    g4: Circle CenterX=0 CenterY=-22.5 CenterZ=0 NormalX=0 NormalY=0 NormalZ=1 AngleXU=0 Radius=8.5
    g5: LineSegment StartX=0 StartY=-22.5 StartZ=0 EndX=-22 EndY=-22.5 EndZ=0
    g6: LineSegment StartX=0 StartY=-22.5 StartZ=0 EndX=22 EndY=-22.5 EndZ=0
    g7: Circle CenterX=-22 CenterY=-22.5 CenterZ=0 NormalX=0 NormalY=0 NormalZ=1 AngleXU=0 Radius=2
    g8: Circle CenterX=22 CenterY=-22.5 CenterZ=0 NormalX=0 NormalY=0 NormalZ=1 AngleXU=0 Radius=2
  constraints (23):
    c: Coincident(g0,g1)
    c: Coincident(g1,g2)
    c: Coincident(g2,g3)
    c: Coincident(g3,g0)
    c: Horizontal(g0)
    c: Vertical(g1)
    c: Symmetric(g2,g1,g-2)
    c: Symmetric(g2,g0,g-1)
    c: DistanceX(g2,g2) = 89
    c: DistanceY(g3,g3) = 89
    c: PointOnObject(g4,g-2)
    c: Diameter(g4) = 17
    c: DistanceY(g1,g4) = 22
    c: Coincident(g5,g4)
    c: Horizontal(g5)
    c: Coincident(g6,g4)
    c: Horizontal(g6)
    c: Equal(g6,g5)
    c: Coincident(g7,g5)
    c: Diameter(g7) = 4
    c: Coincident(g8,g6)
    c: Equal(g8,g7)
    c: DistanceX(g6,g6) = 22
FEATURE [PartDesign::Pad] Pad012
  AlongSketchNormal = false
  Direction = (0,0,1)
  Length = 4.7
  Length2 = 100
  Profile = -> Sketch016
  Type = 0
  expr: Length = <<Parameters>>.PlateThickness
FEATURE [PartDesign::Fillet] Fillet002
  Base = -> Pad009 [Edge44,Edge41]
  BaseFeature = -> Pad009
  Placement = pos=(0,0,0) rot=(1,0,0;1.5708rad)
  Radius = 3
  SupportTransform = false
  UseAllEdges = false
FEATURE [PartDesign::Fillet] Fillet003
  Base = -> Pad010 [Edge44,Edge41]
  BaseFeature = -> Pad010
  Placement = pos=(0,0,0) rot=(1,0,0;1.5708rad)
  Radius = 3
  SupportTransform = false
  UseAllEdges = false
FEATURE [PartDesign::Fillet] Fillet004
  Base = -> Pad011 [Edge38,Edge41]
  BaseFeature = -> Pad011
  Placement = pos=(0,0,0) rot=(1,0,0;1.5708rad)
  Radius = 3
  SupportTransform = false
  UseAllEdges = false
FEATURE [PartDesign::FeatureBase] Clone001
  BaseFeature = -> Body008
FEATURE [PartDesign::Body] Body014  label="LC_Bottom"
  BaseFeature = -> Body008
  Group = -> [Clone001]
  Origin = -> Origin014
  Placement = pos=(535,-80.5,0) rot=(0,0,1;0rad)
  Tip = -> Clone001
  expr: .Placement.Base.x = <<Parameters>>.Width + 100mm + <<Parameters>>.Width + 5 * <<Parameters>>.LCdistance + <<Parameters>>.Length + <<Parameters>>.Width + <<Parameters>>.Length
  expr: .Placement.Base.y = -(<<Parameters>>.Length + <<Parameters>>.LCdistance - 6.5mm)
FEATURE [Part::Part2DObjectPython] Shape2DView  label="Shape_Bottom"  # Draft 2D object (typed FeaturePython)
  AutoUpdate = true
  Base = -> Body014
  Clip = false
  FuseArch = false
  HiddenLines = false
  InPlace = true
  OnlySolids = false
  Projection = (0,0,1)
  ProjectionMode = 0
  SegmentLength = 0.05
  Tessellation = false
  VisibleOnly = false
FEATURE [Sketcher::SketchObject] Sketch017
  FullyConstrained = true
  MapMode = 5
  Placement = pos=(0,0,0) rot=(1,0,0;1.5708rad)
  Support = -> [XZ_Plane020]
  sketch-geometry (10):
    g0: LineSegment StartX=0 StartY=0 StartZ=0 EndX=-36 EndY=0 EndZ=0
    g1: LineSegment StartX=-36 StartY=0 StartZ=0 EndX=-36 EndY=66.5 EndZ=0
    g2: LineSegment StartX=-35 StartY=1 StartZ=0 EndX=0 EndY=1 EndZ=0
    g3: LineSegment StartX=0 StartY=1 StartZ=0 EndX=0 EndY=0 EndZ=0
    g4: LineSegment StartX=-35 StartY=1 StartZ=0 EndX=-35 EndY=65.5 EndZ=0
    g5: LineSegment StartX=-35 StartY=65.5 StartZ=0 EndX=-33.5 EndY=65.5 EndZ=0
    g6: LineSegment StartX=-33.5 StartY=65.5 StartZ=0 EndX=-33.5 EndY=77.5 EndZ=0
    g7: LineSegment StartX=-33.5 StartY=77.5 StartZ=0 EndX=-34.5 EndY=77.5 EndZ=0
    g8: LineSegment StartX=-34.5 StartY=77.5 StartZ=0 EndX=-34.5 EndY=66.5 EndZ=0
    g9: LineSegment StartX=-34.5 StartY=66.5 StartZ=0 EndX=-36 EndY=66.5 EndZ=0
  constraints (29):
    c: Coincident(g-1,g0)
    c: PointOnObject(g0,g-1)
    c: Coincident(g0,g1)
    c: PointOnObject(g2,g-2)
    c: Horizontal(g2)
    c: Coincident(g2,g3)
    c: Coincident(g3,g0)
    c: DistanceX(g0,g0) = 36
    c: DistanceY(g-1,g1) = 66.5
    c: Coincident(g2,g4)
    c: Parallel(g4,g1)
    c: DistanceX(g1,g4) = 1
    c: Vertical(g1)
    c: Coincident(g4,g5)
    c: Horizontal(g5)
    c: Coincident(g5,g6)
    c: Vertical(g6)
    c: Coincident(g6,g7)
    c: Horizontal(g7)
    c: Coincident(g7,g8)
    c: Vertical(g8)
    c: Coincident(g8,g9)
    c: Horizontal(g9)
    c: DistanceY(g6,g6) = 12
    c: DistanceY(g5,g8) = 1
    c: DistanceX(g7,g7) = 1
    c: Coincident(g9,g1)
    c: DistanceX(g9,g9) = 1.5
    c: DistanceY(g3,g3) = 1
FEATURE [PartDesign::Revolution] Revolution004
  Angle = 360
  Axis = (0,-2e-16,1)
  Base = (0,0,0)
  Placement = pos=(0,0,0) rot=(1,0,0;1.5708rad)
  Profile = -> Sketch017
  ReferenceAxis = -> Sketch017 [V_Axis]
FEATURE [PartDesign::Body] Body020  label="Jar (0,2 L)"
  Group = -> [Sketch017,Revolution004]
  Origin = -> Origin020
  Placement = pos=(0,0,3) rot=(0,0,1;0rad)
  Tip = -> Revolution004
FEATURE [Sketcher::SketchObject] Sketch018
  ExternalGeometry = -> [Fillet004]
  FullyConstrained = true
  MapMode = 5
  Placement = pos=(0,0,0) rot=(-1,0,0;1.5708rad)
  Support = -> [Fillet004]
  sketch-geometry (4):
    g0: Circle CenterX=30.02 CenterY=-44.49 CenterZ=0 NormalX=0 NormalY=0 NormalZ=1 AngleXU=0 Radius=2
    g1: Circle CenterX=-30.02 CenterY=-44.49 CenterZ=0 NormalX=0 NormalY=0 NormalZ=1 AngleXU=0 Radius=2
    g2: Circle CenterX=29.8 CenterY=32.1 CenterZ=0 NormalX=0 NormalY=0 NormalZ=1 AngleXU=0 Radius=2
    g3: Circle CenterX=-29.8 CenterY=32.1 CenterZ=0 NormalX=0 NormalY=0 NormalZ=1 AngleXU=0 Radius=2
  constraints (10):
    c: Diameter(g0) = 4
    c: DistanceY(g-3,g0) = 6.51
    c: DistanceX(g0,g-3) = 6.78
    c: Equal(g1,g0)
    c: DistanceX(g-4,g2) = 3
    c: DistanceY(g2,g-4) = 14.2
    c: Equal(g2,g0)
    c: Equal(g3,g2)
    c: Symmetric(g3,g2,g-2)
    c: Symmetric(g1,g0,g-2)
FEATURE [PartDesign::Pocket] Pocket
  BaseFeature = -> Fillet004
  Direction = (0,-1,-2e-16)
  Length = 5
  Length2 = 5
  Placement = pos=(0,0,0) rot=(1,0,0;1.5708rad)
  Profile = -> Sketch018
  ReferenceAxis = -> Sketch018 [N_Axis]
  Type = 1
FEATURE [PartDesign::Body] Body011  label="Side_Left"
  Group = -> [Sketch015,Pad011,Fillet004,Sketch018,Pocket]
  Origin = -> Origin011
  Placement = pos=(-41.5,0,48) rot=(0,0,1;1.5708rad)
  Tip = -> Pocket
  expr: .Placement.Base.x = -(<<Parameters>>.Width / 2)
FEATURE [PartDesign::FeatureBase] Clone
  BaseFeature = -> Body011
  Placement = pos=(-39,-3.5e-14,48) rot=(0,0,1;1.5708rad)
FEATURE [PartDesign::Body] Body012  label="Side_Right (clone)"
  BaseFeature = -> Body011
  Group = -> [Clone]
  Origin = -> Origin012
  Placement = pos=(75.8,0,0) rot=(0,0,1;0rad)
  Tip = -> Clone
  expr: .Placement.Base.x = <<Parameters>>.Width / 2 + 39mm - <<Parameters>>.PlateThickness
FEATURE [PartDesign::FeatureBase] Clone004
  BaseFeature = -> Body011
FEATURE [PartDesign::Body] Body017  label="LC_Side_Left"
  BaseFeature = -> Body011
  Group = -> [Clone004]
  Origin = -> Origin017
  Placement = pos=(270,0,0) rot=(0,0.707107,0.707107;3.14159rad)
  Tip = -> Clone004
  expr: .Placement.Base.x = <<Parameters>>.Width + 100mm + <<Parameters>>.Width + <<Parameters>>.LCdistance
FEATURE [PartDesign::FeatureBase] Clone005
  BaseFeature = -> Body017
FEATURE [PartDesign::Body] Body018  label="LC_Side_Right"
  BaseFeature = -> Body017
  Group = -> [Clone005]
  Origin = -> Origin018
  Placement = pos=(444,0,0) rot=(-1,0,0;1.5708rad)
  Tip = -> Clone005
  expr: .Placement.Base.x = <<Parameters>>.Width + 100mm + <<Parameters>>.Width + 3 * <<Parameters>>.LCdistance + <<Parameters>>.Length + <<Parameters>>.Width
FEATURE [Part::Part2DObjectPython] Shape2DView003  label="Shape_Side_Left"  # Draft 2D object (typed FeaturePython)
  AutoUpdate = true
  Base = -> Body017
  Clip = false
  FuseArch = false
  HiddenLines = false
  InPlace = true
  OnlySolids = false
  Projection = (0,0,1)
  ProjectionMode = 0
  SegmentLength = 0.05
  Tessellation = false
  VisibleOnly = false
FEATURE [Part::Part2DObjectPython] Shape2DView004  label="Shape_Side_Right"  # Draft 2D object (typed FeaturePython)
  AutoUpdate = true
  Base = -> Body018
  Clip = false
  FuseArch = false
  HiddenLines = false
  InPlace = true
  OnlySolids = false
  Projection = (0,0,1)
  ProjectionMode = 0
  SegmentLength = 0.05
  Tessellation = false
  VisibleOnly = false
FEATURE [Sketcher::SketchObject] Sketch019
  ExternalGeometry = -> [Fillet003]
  FullyConstrained = true
  MapMode = 5
  Placement = pos=(0,0,0) rot=(-1,0,0;1.5708rad)
  Support = -> [Fillet003]
  sketch-geometry (2):
    g0: Circle CenterX=-21.5 CenterY=-37 CenterZ=0 NormalX=0 NormalY=0 NormalZ=1 AngleXU=0 Radius=2
    g1: Circle CenterX=-30 CenterY=41.1 CenterZ=0 NormalX=0 NormalY=0 NormalZ=1 AngleXU=0 Radius=2
  constraints (6):
    c: Diameter(g0) = 4
    c: DistanceY(g-3,g0) = 14
    c: DistanceX(g-3,g0) = 20
    c: Equal(g1,g0)
    c: DistanceX(g1,g-4) = 3.2
    c: DistanceY(g1,g-4) = 5.2
FEATURE [PartDesign::Pocket] Pocket001
  BaseFeature = -> Fillet003
  Direction = (0,-1,-2e-16)
  Length = 5
  Length2 = 5
  Placement = pos=(0,0,0) rot=(1,0,0;1.5708rad)
  Profile = -> Sketch019
  ReferenceAxis = -> Sketch019 [N_Axis]
  Type = 1
FEATURE [PartDesign::Mirrored] Mirrored
  BaseFeature = -> Pocket001
  MirrorPlane = -> Sketch019 [V_Axis]
  Originals = -> [Pocket001]
  Placement = pos=(0,0,0) rot=(1,0,0;1.5708rad)
FEATURE [PartDesign::Body] Body010  label="Back"
  Group = -> [Sketch014,Pad010,Fillet003,Sketch019,Pocket001,Mirrored]
  Origin = -> Origin010
  Placement = pos=(0,41.5,48) rot=(0,0,1;0rad)
  Tip = -> Mirrored
  expr: .Placement.Base.y = <<Parameters>>.Length / 2
FEATURE [PartDesign::FeatureBase] Clone003
  BaseFeature = -> Body010
FEATURE [PartDesign::Body] Body016  label="LC_Back"
  BaseFeature = -> Body010
  Group = -> [Clone003]
  Origin = -> Origin016
  Placement = pos=(357,0,0) rot=(0,0.707107,0.707107;3.14159rad)
  Tip = -> Clone003
  expr: .Placement.Base.x = <<Parameters>>.Width + 100mm + <<Parameters>>.Width + 2 * <<Parameters>>.LCdistance + <<Parameters>>.Length
FEATURE [Part::Part2DObjectPython] Shape2DView002  label="Shape_Back"  # Draft 2D object (typed FeaturePython)
  AutoUpdate = true
  Base = -> Body016
  Clip = false
  FuseArch = false
  HiddenLines = false
  InPlace = true
  OnlySolids = false
  Projection = (0,0,1)
  ProjectionMode = 0
  SegmentLength = 0.05
  Tessellation = false
  VisibleOnly = false
FEATURE [Sketcher::SketchObject] Sketch020
  ExternalGeometry = -> [Fillet002]
  FullyConstrained = true
  MapMode = 5
  Placement = pos=(0,-4.7,0) rot=(1,0,0;1.5708rad)
  Support = -> [Fillet002]
  sketch-geometry (2):
    g0: Circle CenterX=-21.5 CenterY=37 CenterZ=0 NormalX=0 NormalY=0 NormalZ=1 AngleXU=0 Radius=2
    g1: Circle CenterX=-30 CenterY=-41.1 CenterZ=0 NormalX=0 NormalY=0 NormalZ=1 AngleXU=0 Radius=2
  constraints (6):
    c: Diameter(g0) = 4
    c: DistanceY(g0,g-3) = 14
    c: DistanceX(g-3,g0) = 20
    c: DistanceX(g1,g-4) = 3.2
    c: DistanceY(g-4,g1) = 5.2
    c: Equal(g1,g0)
FEATURE [PartDesign::Pocket] Pocket002
  BaseFeature = -> Fillet002
  Direction = (0,1,-2e-16)
  Length = 5
  Length2 = 5
  Placement = pos=(0,0,0) rot=(1,0,0;1.5708rad)
  Profile = -> Sketch020
  ReferenceAxis = -> Sketch020 [N_Axis]
  Type = 1
FEATURE [PartDesign::Mirrored] Mirrored001
  BaseFeature = -> Pocket002
  MirrorPlane = -> Sketch020 [V_Axis]
  Originals = -> [Pocket002]
  Placement = pos=(0,0,0) rot=(1,0,0;1.5708rad)
FEATURE [PartDesign::Body] Body009  label="Front"
  Group = -> [Sketch013,Pad009,Fillet002,Sketch020,Pocket002,Mirrored001]
  Origin = -> Origin009
  Placement = pos=(0,-36.8,48) rot=(0,0,1;0rad)
  Tip = -> Mirrored001
  expr: .Placement.Base.y = -(<<Parameters>>.Length / 2 - <<Parameters>>.PlateThickness)
FEATURE [PartDesign::FeatureBase] Clone002
  BaseFeature = -> Body009
FEATURE [PartDesign::Body] Body015  label="LC_Front"
  BaseFeature = -> Body009
  Group = -> [Clone002]
  Origin = -> Origin015
  Placement = pos=(183,0,0) rot=(-1,0,0;1.5708rad)
  Tip = -> Clone002
  expr: .Placement.Base.x = <<Parameters>>.Width + 100mm
FEATURE [Part::Part2DObjectPython] Shape2DView001  label="Shape_Front"  # Draft 2D object (typed FeaturePython)
  AutoUpdate = true
  Base = -> Body015
  Clip = false
  FuseArch = false
  HiddenLines = false
  InPlace = true
  OnlySolids = false
  Projection = (0,0,1)
  ProjectionMode = 0
  SegmentLength = 0.05
  Tessellation = false
  VisibleOnly = false
FEATURE [Sketcher::SketchObject] Sketch021
  ExternalGeometry = -> [Pad012]
  FullyConstrained = true
  MapMode = 5
  Placement = pos=(0,0,4.7) rot=(0,0,1;0rad)
  Support = -> [Pad012]
  sketch-geometry (1):
    g0: Circle CenterX=-27 CenterY=29.1 CenterZ=0 NormalX=0 NormalY=0 NormalZ=1 AngleXU=0 Radius=2
  constraints (3):
    c: Diameter(g0) = 4
    c: DistanceX(g-3,g0) = 17.5
    c: DistanceY(g0,g-3) = 15.4
FEATURE [PartDesign::Pocket] Pocket003
  BaseFeature = -> Pad012
  Direction = (0,0,-1)
  Length = 5
  Length2 = 5
  Profile = -> Sketch021
  ReferenceAxis = -> Sketch021 [N_Axis]
  Type = 1
FEATURE [PartDesign::Mirrored] Mirrored002
  BaseFeature = -> Pocket003
  MirrorPlane = -> Sketch021 [V_Axis]
  Originals = -> [Pocket003]
FEATURE [PartDesign::Body] Body013  label="Lid"
  Group = -> [Sketch016,Pad012,Sketch021,Pocket003,Mirrored002]
  Origin = -> Origin013
  Placement = pos=(0,0,99) rot=(0,0,1;0rad)
  Tip = -> Mirrored002
  expr: .Placement.Base.z = 99mm + (<<Parameters>>.Height - 102mm) / 2
FEATURE [PartDesign::FeatureBase] Clone006
  BaseFeature = -> Body013
FEATURE [PartDesign::Body] Body019  label="LC_Lid"
  BaseFeature = -> Body013
  Group = -> [Clone006]
  Origin = -> Origin019
  Placement = pos=(535,6.5,0) rot=(0,0,1;0rad)
  Tip = -> Clone006
  expr: .Placement.Base.x = <<Parameters>>.Width + 100mm + <<Parameters>>.Width + 5 * <<Parameters>>.LCdistance + <<Parameters>>.Length + <<Parameters>>.Width + <<Parameters>>.Length
FEATURE [App::DocumentObjectGroup] Group002  label="Lasercut parts"
  Group = -> [Body008,Body009,Body010,Body011,Body012,Body013]
FEATURE [App::DocumentObjectGroup] Group003  label="Lasercut parts (clones)"
  Group = -> [Body015,Body017,Body016,Body018,Body019,Body014]
FEATURE [Part::Part2DObjectPython] Shape2DView005  label="Shape_Lid"  # Draft 2D object (typed FeaturePython)
  AutoUpdate = true
  Base = -> Body019
  Clip = false
  FuseArch = false
  HiddenLines = false
  InPlace = true
  OnlySolids = false
  Projection = (0,0,1)
  ProjectionMode = 0
  SegmentLength = 0.05
  Tessellation = false
  VisibleOnly = false
FEATURE [App::DocumentObjectGroup] Group004  label="Projections for Lasercutting"
  Group = -> [Shape2DView001,Shape2DView003,Shape2DView002,Shape2DView004,Shape2DView005,Shape2DView,Group003]
FEATURE [Sketcher::SketchObject] Sketch037
  FullyConstrained = true
  MapMode = 5
  Placement = pos=(0,0,0) rot=(1,0,0;1.5708rad)
  Support = -> [XZ_Plane024]
  sketch-geometry (26):
    g0: Circle CenterX=0 CenterY=0 CenterZ=0 NormalX=0 NormalY=0 NormalZ=1 AngleXU=0 Radius=2
    g1: LineSegment StartX=4.5 StartY=-4 StartZ=0 EndX=-4.3 EndY=-4 EndZ=0
    g2: LineSegment StartX=-14.8 StartY=11.74 StartZ=0 EndX=-9.8 EndY=11.74 EndZ=0
    g3: LineSegment StartX=-9.8 StartY=11.74 StartZ=0 EndX=-9.8 EndY=9.5 EndZ=0
    g4: LineSegment StartX=-9.8 StartY=9.5 StartZ=0 EndX=2.5 EndY=9.5 EndZ=0
    g5: LineSegment StartX=2.5 StartY=9.5 StartZ=0 EndX=2.5 EndY=5 EndZ=0
    g6: LineSegment StartX=2.5 StartY=5 StartZ=0 EndX=4.5 EndY=5 EndZ=0
    g7: LineSegment StartX=4.5 StartY=5 StartZ=0 EndX=4.5 EndY=-4 EndZ=0
    g8: LineSegment StartX=-14.8 StartY=3.24 StartZ=0 EndX=-14.8 EndY=7.49 EndZ=0
    g9: LineSegment StartX=-14.8 StartY=11.74 StartZ=0 EndX=-14.8 EndY=7.49 EndZ=0
    g10: LineSegment StartX=-14.8 StartY=3.24 StartZ=0 EndX=-4.3 EndY=3.24 EndZ=0
    g11: LineSegment StartX=-4.3 StartY=3.24 StartZ=0 EndX=-4.3 EndY=-4 EndZ=0
    g12: LineSegment StartX=-3.2909 StartY=0 StartZ=0 EndX=-1.64545 EndY=-2.85 EndZ=0
    g13: LineSegment StartX=-1.64545 StartY=-2.85 StartZ=0 EndX=1.64545 EndY=-2.85 EndZ=0
    g14: LineSegment StartX=1.64545 StartY=-2.85 StartZ=0 EndX=3.2909 EndY=4e-16 EndZ=0
    g15: LineSegment StartX=3.2909 StartY=4e-16 StartZ=0 EndX=1.64545 EndY=2.85 EndZ=0
    g16: LineSegment StartX=1.64545 StartY=2.85 StartZ=0 EndX=-1.64545 EndY=2.85 EndZ=0
    g17: LineSegment StartX=-1.64545 StartY=2.85 StartZ=0 EndX=-3.2909 EndY=0 EndZ=0
    g18: Circle CenterX=0 CenterY=0 CenterZ=0 NormalX=0 NormalY=0 NormalZ=1 AngleXU=0 Radius=3.2909
    g19: LineSegment StartX=-4.0909 StartY=-4e-16 StartZ=0 EndX=-2.04545 EndY=-3.54282 EndZ=0
    g20: LineSegment StartX=-2.04545 StartY=-3.54282 StartZ=0 EndX=2.04545 EndY=-3.54282 EndZ=0
    g21: LineSegment StartX=2.04545 StartY=-3.54282 StartZ=0 EndX=4.0909 EndY=0 EndZ=0
    g22: LineSegment StartX=4.0909 StartY=0 StartZ=0 EndX=2.04545 EndY=3.54282 EndZ=0
    g23: LineSegment StartX=2.04545 StartY=3.54282 StartZ=0 EndX=-2.04545 EndY=3.54282 EndZ=0
    g24: LineSegment StartX=-2.04545 StartY=3.54282 StartZ=0 EndX=-4.0909 EndY=-4e-16 EndZ=0
    g25: Circle CenterX=0 CenterY=0 CenterZ=0 NormalX=0 NormalY=0 NormalZ=1 AngleXU=0 Radius=4.0909
  constraints (67):
    c: Coincident(g0,g-1)
    c: Diameter(g0) = 4
    c: Horizontal(g1)
    c: Horizontal(g2)
    c: Coincident(g2,g3)
    c: Vertical(g3)
    c: Coincident(g3,g4)
    c: Horizontal(g4)
    c: Coincident(g4,g5)
    c: Vertical(g5)
    c: Coincident(g5,g6)
    c: Horizontal(g6)
    c: Coincident(g6,g7)
    c: Coincident(g7,g1)
    c: Vertical(g7)
    c: Vertical(g8)
    c: Coincident(g9,g2)
    c: Coincident(g9,g8)
    c: Vertical(g9)
    c: Equal(g8,g9)
    c: DistanceY(g8,g8) = 4.25
    c: DistanceY(g1,g-1) = 4
    c: DistanceX(g-1,g1) = 4.5
    c: DistanceY(g1,g8) = 7.24
    c: DistanceY(g7,g7) = 9
    c: DistanceX(g6,g6) = 2
    c: DistanceY(g5,g5) = 4.5
    c: DistanceX(g2,g2) = 5
    c: DistanceX(g4,g4) = 12.3
    c: Coincident(g8,g10)
    c: Horizontal(g10)
    c: Coincident(g10,g11)
    c: Coincident(g11,g1)
    c: Vertical(g11)
    c: Coincident(g12,g13)
    c: Coincident(g13,g14)
    c: Coincident(g14,g15)
    c: Coincident(g15,g16)
    c: Coincident(g16,g17)
    c: Coincident(g17,g12)
    c: Equal(g12, g13-g17) x5
    c: PointOnObject(g12,g18)
    c: PointOnObject(g13,g18)
    c: PointOnObject(g14,g18)
    c: PointOnObject(g15,g18)
    c: PointOnObject(g16,g18)
    c: PointOnObject(g17,g18)
    c: Coincident(g18,g0)
    c: PointOnObject(g17,g-1)
    c: DistanceY(g12,g16) = 5.7
    c: Coincident(g19,g20)
    c: Coincident(g20,g21)
    c: Coincident(g21,g22)
    c: Coincident(g22,g23)
    c: Coincident(g23,g24)
    c: Coincident(g24,g19)
    c: Equal(g19, g20-g24) x5
    c: PointOnObject(g19,g25)
    c: PointOnObject(g20,g25)
    c: PointOnObject(g21,g25)
    c: PointOnObject(g22,g25)
    c: PointOnObject(g23,g25)
    c: PointOnObject(g24,g25)
    c: Coincident(g25,g0)
    c: PointOnObject(g24,g-1)
    c: DistanceX(g19,g12) = 0.8
    c: DistanceX(g10,g10) = 10.5
FEATURE [PartDesign::Pad] Pad022
  Direction = (0,-1,-2e-16)
  Length = 1.3
  Length2 = 10
  Placement = pos=(0,0,0) rot=(1,0,0;1.5708rad)
  Profile = -> Sketch037
  ReferenceAxis = -> Sketch037 [N_Axis]
  Type = 0
FEATURE [Sketcher::SketchObject] Sketch038
  FullyConstrained = true
  MapMode = 5
  Placement = pos=(0,-1.3,0) rot=(1,0,0;1.5708rad)
  Support = -> [Pad022]
  sketch-geometry (14):
    g0: LineSegment StartX=-3.2909 StartY=0 StartZ=0 EndX=-1.64545 EndY=-2.85 EndZ=0
    g1: LineSegment StartX=-1.64545 StartY=-2.85 StartZ=0 EndX=1.64545 EndY=-2.85 EndZ=0
    g2: LineSegment StartX=1.64545 StartY=-2.85 StartZ=0 EndX=3.2909 EndY=0 EndZ=0
    g3: LineSegment StartX=3.2909 StartY=0 StartZ=0 EndX=1.64545 EndY=2.85 EndZ=0
    g4: LineSegment StartX=1.64545 StartY=2.85 StartZ=0 EndX=-1.64545 EndY=2.85 EndZ=0
    g5: LineSegment StartX=-1.64545 StartY=2.85 StartZ=0 EndX=-3.2909 EndY=0 EndZ=0
    g6: Circle CenterX=0 CenterY=0 CenterZ=0 NormalX=0 NormalY=0 NormalZ=1 AngleXU=0 Radius=3.2909
    g7: LineSegment StartX=-4.0909 StartY=0 StartZ=0 EndX=-2.04545 EndY=-3.54282 EndZ=0
    g8: LineSegment StartX=-2.04545 StartY=-3.54282 StartZ=0 EndX=2.04545 EndY=-3.54282 EndZ=0
    g9: LineSegment StartX=2.04545 StartY=-3.54282 StartZ=0 EndX=4.0909 EndY=5.032e-13 EndZ=0
    g10: LineSegment StartX=4.0909 StartY=5.032e-13 StartZ=0 EndX=2.04545 EndY=3.54282 EndZ=0
    g11: LineSegment StartX=2.04545 StartY=3.54282 StartZ=0 EndX=-2.04545 EndY=3.54282 EndZ=0
    g12: LineSegment StartX=-2.04545 StartY=3.54282 StartZ=0 EndX=-4.0909 EndY=0 EndZ=0
    g13: Circle CenterX=0 CenterY=0 CenterZ=0 NormalX=0 NormalY=0 NormalZ=1 AngleXU=0 Radius=4.0909
  constraints (32):
    c: Coincident(g0,g1)
    c: Coincident(g1,g2)
    c: Coincident(g2,g3)
    c: Coincident(g3,g4)
    c: Coincident(g4,g5)
    c: Coincident(g5,g0)
    c: Equal(g0, g1-g5) x5
    c: PointOnObject(g0,g6)
    c: PointOnObject(g1,g6)
    c: PointOnObject(g2,g6)
    c: PointOnObject(g3,g6)
    c: PointOnObject(g4,g6)
    c: PointOnObject(g5,g6)
    c: Coincident(g6,g-1)
    c: PointOnObject(g5,g-1)
    c: DistanceY(g0,g4) = 5.7
    c: Coincident(g7,g8)
    c: Coincident(g8,g9)
    c: Coincident(g9,g10)
    c: Coincident(g10,g11)
    c: Coincident(g11,g12)
    c: Coincident(g12,g7)
    c: Equal(g7, g8-g12) x5
    c: PointOnObject(g7,g13)
    c: PointOnObject(g8,g13)
    c: PointOnObject(g9,g13)
    c: PointOnObject(g10,g13)
    c: PointOnObject(g11,g13)
    c: PointOnObject(g12,g13)
    c: Coincident(g13,g6)
    c: PointOnObject(g12,g-1)
    c: DistanceX(g7,g0) = 0.8
FEATURE [PartDesign::Pad] Pad023
  BaseFeature = -> Pad022
  Direction = (0,-1,-2e-16)
  Length = 2.7
  Length2 = 10
  Placement = pos=(0,0,0) rot=(1,0,0;1.5708rad)
  Profile = -> Sketch038
  ReferenceAxis = -> Sketch038 [N_Axis]
  Type = 0
FEATURE [Sketcher::SketchObject] Sketch039
  ExternalGeometry = -> [Pad023]
  FullyConstrained = false
  MapMode = 5
  Placement = pos=(0,-1.3,0) rot=(1,0,0;1.5708rad)
  Support = -> [Pad023]
  sketch-geometry (8):
    g0: LineSegment StartX=-2 StartY=9.5 StartZ=0 EndX=-9 EndY=9.5 EndZ=0
    g1: LineSegment StartX=-9 StartY=9.5 StartZ=0 EndX=-9 EndY=7.5 EndZ=0
    g2: LineSegment StartX=-9 StartY=7.5 StartZ=0 EndX=-2 EndY=7.5 EndZ=0
    g3: LineSegment StartX=-2 StartY=7.5 StartZ=0 EndX=-2 EndY=9.5 EndZ=0
    g4: LineSegment StartX=-9 StartY=8.7441 StartZ=0 EndX=-7 EndY=8.7441 EndZ=0
    g5: LineSegment StartX=-7 StartY=8.7441 StartZ=0 EndX=-5.5 EndY=8.7441 EndZ=0
    g6: LineSegment StartX=-5.5 StartY=8.7441 StartZ=0 EndX=-4 EndY=8.7441 EndZ=0
    g7: LineSegment StartX=-4 StartY=8.7441 StartZ=0 EndX=-2 EndY=8.7441 EndZ=0
  constraints (24):
    c: Coincident(g0,g1)
    c: Coincident(g1,g2)
    c: Coincident(g2,g3)
    c: Coincident(g3,g0)
    c: Horizontal(g0)
    c: Horizontal(g2)
    c: Vertical(g1)
    c: Vertical(g3)
    c: PointOnObject(g0,g-3)
    c: PointOnObject(g4,g1)
    c: Horizontal(g4)
    c: Coincident(g4,g5)
    c: Horizontal(g5)
    c: Coincident(g5,g6)
    c: Horizontal(g6)
    c: Coincident(g6,g7)
    c: PointOnObject(g7,g3)
    c: Horizontal(g7)
    c: Equal(g5,g6)
    c: Equal(g4,g7)
    c: DistanceX(g5,g5) = 1.5
    c: DistanceX(g0,g0) = 7
    c: DistanceX(g0,g-3) = 4.5
    c: DistanceY(g3,g3) = 2
FEATURE [PartDesign::Pad] Pad024
  BaseFeature = -> Pad023
  Direction = (0,-1,-2e-16)
  Length = 10
  Length2 = 10
  Placement = pos=(0,0,0) rot=(1,0,0;1.5708rad)
  Profile = -> Sketch039
  ReferenceAxis = -> Sketch039 [N_Axis]
  Type = 0
FEATURE [Sketcher::SketchObject] Sketch040
  FullyConstrained = true
  MapMode = 5
  Placement = pos=(0,2.1e-15,9.5) rot=(0,0,1;3.14159rad)
  Support = -> [Pad024]
  sketch-geometry (1):
    g0: Circle CenterX=5.5 CenterY=7.7 CenterZ=0 NormalX=0 NormalY=0 NormalZ=1 AngleXU=0 Radius=2
  constraints (3):
    c: Diameter(g0) = 4
    c: DistanceY(g-1,g0) = 7.7
    c: DistanceX(g-1,g0) = 5.5
FEATURE [PartDesign::Pocket] Pocket010
  BaseFeature = -> Pad024
  Direction = (0,2e-16,-1)
  Length = 2
  Length2 = 5
  Placement = pos=(0,0,0) rot=(1,0,0;1.5708rad)
  Profile = -> Sketch040
  ReferenceAxis = -> Sketch040 [N_Axis]
  Type = 0
FEATURE [Sketcher::SketchObject] Sketch041
  ExternalGeometry = -> [Pocket010]
  FullyConstrained = true
  MapMode = 5
  Placement = pos=(-14.8,0,0) rot=(0.707107,0,-0.707107;3.14159rad)
  Support = -> [Pocket010]
  sketch-geometry (6):
    g0: LineSegment StartX=-11.74 StartY=1.3 StartZ=0 EndX=-3.24 EndY=1.3 EndZ=0
    g1: LineSegment StartX=-3.24 StartY=1.3 StartZ=0 EndX=-3.24 EndY=10.2 EndZ=0
    g2: LineSegment StartX=-3.24 StartY=10.2 StartZ=0 EndX=-11.74 EndY=10.2 EndZ=0
    g3: LineSegment StartX=-11.74 StartY=10.2 StartZ=0 EndX=-11.74 EndY=1.3 EndZ=0
    g4: LineSegment StartX=-7.49 StartY=1.3 StartZ=0 EndX=-7.49 EndY=10.2 EndZ=0
    g5: Circle CenterX=-7.49 CenterY=6.8 CenterZ=0 NormalX=0 NormalY=0 NormalZ=1 AngleXU=0 Radius=2
  constraints (16):
    c: Coincident(g0,g1)
    c: Coincident(g1,g2)
    c: Coincident(g2,g3)
    c: Coincident(g3,g0)
    c: Horizontal(g2)
    c: Vertical(g1)
    c: Vertical(g3)
    c: Coincident(g0,g-3)
    c: Coincident(g0,g-4)
    c: Coincident(g4,g-4)
    c: PointOnObject(g4,g2)
    c: Vertical(g4)
    c: PointOnObject(g5,g4)
    c: Diameter(g5) = 4
    c: DistanceY(g-1,g5) = 6.8
    c: DistanceY(g5,g1) = 3.4
FEATURE [PartDesign::Pad] Pad025
  BaseFeature = -> Pocket010
  Direction = (-1,0,-2e-16)
  Length = 5
  Length2 = 10
  Placement = pos=(0,0,0) rot=(1,0,0;1.5708rad)
  Profile = -> Sketch041
  ReferenceAxis = -> Sketch041 [N_Axis]
  Reversed = true
  Type = 0
FEATURE [Sketcher::SketchObject] Sketch042
  ExternalGeometry = -> [Pad025]
  FullyConstrained = true
  MapMode = 5
  Placement = pos=(-14.8,1e-16,-3e-15) rot=(0.707107,0,-0.707107;3.14159rad)
  Support = -> [Pad025]
  sketch-geometry (16):
    g0: LineSegment StartX=-4.54 StartY=8.50318 StartZ=0 EndX=-7.49 EndY=10.2064 EndZ=0
    g1: LineSegment StartX=-7.49 StartY=10.2064 StartZ=0 EndX=-10.44 EndY=8.50318 EndZ=0
    g2: LineSegment StartX=-10.44 StartY=8.50318 StartZ=0 EndX=-10.44 EndY=5.09682 EndZ=0
    g3: LineSegment StartX=-10.44 StartY=5.09682 StartZ=0 EndX=-7.49 EndY=3.39363 EndZ=0
    g4: LineSegment StartX=-7.49 StartY=3.39363 StartZ=0 EndX=-4.54 EndY=5.09682 EndZ=0
    g5: LineSegment StartX=-4.54 StartY=5.09682 StartZ=0 EndX=-4.54 EndY=8.50318 EndZ=0
    g6: Circle CenterX=-7.49 CenterY=6.8 CenterZ=0 NormalX=0 NormalY=0 NormalZ=1 AngleXU=0 Radius=3.40637
    g7: LineSegment StartX=-10.44 StartY=8.50318 StartZ=0 EndX=-11.74 EndY=8.50318 EndZ=0
    g8: LineSegment StartX=-11.74 StartY=8.50318 StartZ=0 EndX=-11.74 EndY=10.2 EndZ=0
    g9: LineSegment StartX=-11.74 StartY=10.2 StartZ=0 EndX=-3.24 EndY=10.2 EndZ=0
    g10: LineSegment StartX=-3.24 StartY=10.2 StartZ=0 EndX=-3.24 EndY=8.50318 EndZ=0
    g11: LineSegment StartX=-3.24 StartY=8.50318 StartZ=0 EndX=-4.54 EndY=8.50318 EndZ=0
    g12: LineSegment StartX=-4.54 StartY=8.50318 StartZ=0 EndX=-4.54 EndY=5.09682 EndZ=0
    g13: LineSegment StartX=-4.54 StartY=5.09682 StartZ=0 EndX=-7.49 EndY=3.39363 EndZ=0
    g14: LineSegment StartX=-7.49 StartY=3.39363 StartZ=0 EndX=-10.44 EndY=5.09682 EndZ=0
    g15: LineSegment StartX=-10.44 StartY=5.09682 StartZ=0 EndX=-10.44 EndY=8.50318 EndZ=0
  constraints (36):
    c: Coincident(g0,g1)
    c: Coincident(g1,g2)
    c: Coincident(g2,g3)
    c: Coincident(g3,g4)
    c: Coincident(g4,g5)
    c: Coincident(g5,g0)
    c: Equal(g0, g1-g5) x5
    c: PointOnObject(g0,g6)
    c: PointOnObject(g1,g6)
    c: PointOnObject(g2,g6)
    c: PointOnObject(g3,g6)
    c: PointOnObject(g4,g6)
    c: PointOnObject(g5,g6)
    c: Coincident(g6,g-3)
    c: Vertical(g5)
    c: DistanceX(g1,g0) = 5.9
    c: Coincident(g1,g7)
    c: PointOnObject(g7,g-6)
    c: Horizontal(g7)
    c: Coincident(g7,g8)
    c: Coincident(g8,g-6)
    c: Coincident(g8,g9)
    c: Coincident(g9,g-5)
    c: Coincident(g9,g10)
    c: PointOnObject(g10,g-5)
    c: Coincident(g10,g11)
    c: Coincident(g11,g0)
    c: Horizontal(g11)
    c: Coincident(g11,g12)
    c: Coincident(g12,g4)
    c: Coincident(g12,g13)
    c: Coincident(g13,g3)
    c: Coincident(g13,g14)
    c: Coincident(g14,g2)
    c: Coincident(g14,g15)
    c: Coincident(g15,g7)
FEATURE [PartDesign::Pocket] Pocket011
  BaseFeature = -> Pad025
  Direction = (1,0,2e-16)
  Length = 0.9
  Length2 = -3.7
  Placement = pos=(0,0,0) rot=(1,0,0;1.5708rad)
  Profile = -> Sketch042
  ReferenceAxis = -> Sketch042 [N_Axis]
  Type = 4
FEATURE [Sketcher::SketchObject] Sketch043
  ExternalGeometry = -> [Pocket011]
  FullyConstrained = true
  MapMode = 5
  Placement = pos=(0,-1.3,0) rot=(1,0,0;1.5708rad)
  Support = -> [Pocket011]
  sketch-geometry (4):
    g0: LineSegment StartX=2.5 StartY=5 StartZ=0 EndX=-2 EndY=5 EndZ=0
    g1: LineSegment StartX=-2 StartY=5 StartZ=0 EndX=-2 EndY=9.5 EndZ=0
    g2: LineSegment StartX=-2 StartY=9.5 StartZ=0 EndX=2.5 EndY=9.5 EndZ=0
    g3: LineSegment StartX=2.5 StartY=9.5 StartZ=0 EndX=2.5 EndY=5 EndZ=0
  constraints (10):
    c: Coincident(g0,g1)
    c: Coincident(g1,g2)
    c: Coincident(g2,g3)
    c: Coincident(g3,g0)
    c: Horizontal(g0)
    c: Horizontal(g2)
    c: Vertical(g1)
    c: Vertical(g3)
    c: Coincident(g0,g-3)
    c: Coincident(g1,g-4)
FEATURE [PartDesign::Pocket] Pocket012
  BaseFeature = -> Pocket011
  Direction = (0,1,-2e-16)
  Length = 5
  Length2 = 5
  Placement = pos=(0,0,0) rot=(1,0,0;1.5708rad)
  Profile = -> Sketch043
  ReferenceAxis = -> Sketch043 [N_Axis]
  Type = 1
FEATURE [PartDesign::Fillet] Fillet005
  Base = -> Pocket012 [Edge52,Edge45,Edge43,Edge40]
  BaseFeature = -> Pocket012
  Placement = pos=(0,0,0) rot=(1,0,0;1.5708rad)
  Radius = 2
  SupportTransform = false
  UseAllEdges = false
FEATURE [PartDesign::Fillet] Fillet006
  Base = -> Fillet005 [Edge43]
  BaseFeature = -> Fillet005
  Placement = pos=(0,0,0) rot=(1,0,0;1.5708rad)
  Radius = 1.7
  SupportTransform = false
  UseAllEdges = false
FEATURE [PartDesign::Fillet] Fillet007
  Base = -> Fillet006 [Edge100,Edge69]
  BaseFeature = -> Fillet006
  Placement = pos=(0,0,0) rot=(1,0,0;1.5708rad)
  Radius = 3
  SupportTransform = false
  UseAllEdges = false
FEATURE [Mesh::Feature] Male_Thread__cut_  label="Male_Thread_(cut)"
  Placement = pos=(-125,-127.5,116) rot=(0,0,1;0rad)
FEATURE [Sketcher::SketchObject] Sketch044
  FullyConstrained = true
  MapMode = 5
  Support = -> [XY_Plane026]
  sketch-geometry (2):
    g0: Circle CenterX=0 CenterY=0 CenterZ=0 NormalX=0 NormalY=0 NormalZ=1 AngleXU=0 Radius=11.5
    g1: Circle CenterX=0 CenterY=0 CenterZ=0 NormalX=0 NormalY=0 NormalZ=1 AngleXU=0 Radius=14.5
  constraints (4):
    c: Coincident(g0,g-1)
    c: Diameter(g0) = 23
    c: Coincident(g1,g0)
    c: Diameter(g1) = 29
FEATURE [PartDesign::Pad] Pad026
  Direction = (0,0,1)
  Length = 1.3
  Length2 = 10
  Profile = -> Sketch044
  ReferenceAxis = -> Sketch044 [N_Axis]
  Type = 0
FEATURE [Sketcher::SketchObject] Sketch045
  FullyConstrained = true
  MapMode = 5
  Support = -> [XY_Plane026]
  sketch-geometry (7):
    g0: Circle CenterX=-22 CenterY=0 CenterZ=0 NormalX=0 NormalY=0 NormalZ=1 AngleXU=0 Radius=2.25
    g1: Circle CenterX=-22 CenterY=0 CenterZ=0 NormalX=0 NormalY=0 NormalZ=1 AngleXU=0 Radius=4.5
    g2: LineSegment StartX=-22.7814 StartY=4.43163 StartZ=0 EndX=-12 EndY=6.33269 EndZ=0
    g3: LineSegment StartX=-12 StartY=6.33269 StartZ=0 EndX=-12 EndY=-6.33269 EndZ=0
    g4: LineSegment StartX=-12 StartY=-6.33269 StartZ=0 EndX=-22.7814 EndY=-4.43163 EndZ=0
    g5: LineSegment StartX=-22.7814 StartY=4.43163 StartZ=0 EndX=-22.7814 EndY=-4.43163 EndZ=0
    g6: ArcOfCircle CenterX=-22 CenterY=0 CenterZ=0 NormalX=0 NormalY=0 NormalZ=1 AngleXU=0 Radius=4.5 StartAngle=1.74533 EndAngle=4.53786
  constraints (17):
    c: PointOnObject(g0,g-1)
    c: Diameter(g0) = 4.5
    c: DistanceX(g0,g-1) = 22
    c: Coincident(g1,g0)
    c: Diameter(g1) = 9
    c: PointOnObject(g2,g1)
    c: Coincident(g2,g3)
    c: Coincident(g3,g4)
    c: Coincident(g5,g2)
    c: Coincident(g5,g4)
    c: Vertical(g5)
    c: Symmetric(g3,g2,g-1)
    c: DistanceX(g2,g-1) = 12
    c: Angle(g5,g2) = 1.74533
    c: Coincident(g6,g0)
    c: Coincident(g6,g4)
    c: Tangent(g6,g2) = 1.5708
FEATURE [PartDesign::Pad] Pad027
  BaseFeature = -> Pad026
  Direction = (0,0,1)
  Length = 1.3
  Length2 = 10
  Profile = -> Sketch045
  ReferenceAxis = -> Sketch045 [N_Axis]
  Type = 0
FEATURE [PartDesign::Mirrored] Mirrored003
  BaseFeature = -> Pad027
  MirrorPlane = -> Sketch045 [V_Axis]
  Originals = -> [Pad027]
FEATURE [PartDesign::Body] Body026  label="Plate_Adapter_for_pump"
  Group = -> [Sketch044,Pad026,Sketch045,Pad027,Mirrored003]
  Origin = -> Origin026
  Placement = pos=(0,-22.5,103.8) rot=(0,0,1;0rad)
  Tip = -> Mirrored003
FEATURE [Mesh::Feature] _DP_Adapter_for_pump  label="3DP_Adapter_for_pump"
FEATURE [Sketcher::SketchObject] Sketch046
  FullyConstrained = true
  MapMode = 5
  Placement = pos=(0,0,0) rot=(1,0,0;1.5708rad)
  Support = -> [XZ_Plane027]
  sketch-geometry (5):
    g0: Circle CenterX=0 CenterY=0 CenterZ=0 NormalX=0 NormalY=0 NormalZ=1 AngleXU=0 Radius=2
    g1: LineSegment StartX=-3.75 StartY=3.2 StartZ=0 EndX=3.75 EndY=3.2 EndZ=0
    g2: LineSegment StartX=3.75 StartY=3.2 StartZ=0 EndX=3.75 EndY=-5.2 EndZ=0
    g3: LineSegment StartX=3.75 StartY=-5.2 StartZ=0 EndX=-3.75 EndY=-5.2 EndZ=0
    g4: LineSegment StartX=-3.75 StartY=-5.2 StartZ=0 EndX=-3.75 EndY=3.2 EndZ=0
  constraints (13):
    c: Coincident(g0,g-1)
    c: Coincident(g1,g2)
    c: Coincident(g2,g3)
    c: Coincident(g3,g4)
    c: Coincident(g4,g1)
    c: Horizontal(g3)
    c: Vertical(g2)
    c: Vertical(g4)
    c: Symmetric(g1,g1,g-2)
    c: DistanceX(g1,g1) = 7.5
    c: DistanceY(g4,g4) = 8.4
    c: Diameter(g0) = 4
    c: DistanceY(g2,g-1) = 5.2
FEATURE [PartDesign::Pad] Pad028
  Direction = (0,-1,-2e-16)
  Length = 4.6
  Length2 = 10
  Placement = pos=(0,0,0) rot=(1,0,0;1.5708rad)
  Profile = -> Sketch046
  ReferenceAxis = -> Sketch046 [N_Axis]
  Type = 0
FEATURE [Sketcher::SketchObject] Sketch047
  ExternalGeometry = -> [Pad028]
  FullyConstrained = true
  MapMode = 5
  Placement = pos=(0,-4.6,0) rot=(1,0,0;1.5708rad)
  Support = -> [Pad028]
  sketch-geometry (16):
    g0: LineSegment StartX=0 StartY=3.40637 StartZ=0 EndX=-2.95 EndY=1.70318 EndZ=0
    g1: LineSegment StartX=-2.95 StartY=1.70318 StartZ=0 EndX=-2.95 EndY=-1.70318 EndZ=0
    g2: LineSegment StartX=-2.95 StartY=-1.70318 StartZ=0 EndX=-4e-16 EndY=-3.40637 EndZ=0
    g3: LineSegment StartX=-4e-16 StartY=-3.40637 StartZ=0 EndX=2.95 EndY=-1.70318 EndZ=0
    g4: LineSegment StartX=2.95 StartY=-1.70318 StartZ=0 EndX=2.95 EndY=1.70318 EndZ=0
    g5: LineSegment StartX=2.95 StartY=1.70318 StartZ=0 EndX=0 EndY=3.40637 EndZ=0
    g6: Circle CenterX=0 CenterY=0 CenterZ=0 NormalX=0 NormalY=0 NormalZ=1 AngleXU=0 Radius=3.40637
    g7: LineSegment StartX=2.95 StartY=1.70318 StartZ=0 EndX=3.75 EndY=1.70318 EndZ=0
    g8: LineSegment StartX=3.75 StartY=1.70318 StartZ=0 EndX=3.75 EndY=3.2 EndZ=0
    g9: LineSegment StartX=3.75 StartY=3.2 StartZ=0 EndX=-3.75 EndY=3.2 EndZ=0
    g10: LineSegment StartX=-3.75 StartY=3.2 StartZ=0 EndX=-3.75 EndY=1.70318 EndZ=0
    g11: LineSegment StartX=-3.75 StartY=1.70318 StartZ=0 EndX=-2.95 EndY=1.70318 EndZ=0
    g12: LineSegment StartX=-2.95 StartY=1.70318 StartZ=0 EndX=-2.95 EndY=-1.70318 EndZ=0
    g13: LineSegment StartX=-2.95 StartY=-1.70318 StartZ=0 EndX=-4e-16 EndY=-3.40637 EndZ=0
    g14: LineSegment StartX=-4e-16 StartY=-3.40637 StartZ=0 EndX=2.95 EndY=-1.70318 EndZ=0
    g15: LineSegment StartX=2.95 StartY=-1.70318 StartZ=0 EndX=2.95 EndY=1.70318 EndZ=0
  constraints (36):
    c: Coincident(g0,g1)
    c: Coincident(g1,g2)
    c: Coincident(g2,g3)
    c: Coincident(g3,g4)
    c: Coincident(g4,g5)
    c: Coincident(g5,g0)
    c: Equal(g0, g1-g5) x5
    c: PointOnObject(g0,g6)
    c: PointOnObject(g1,g6)
    c: PointOnObject(g2,g6)
    c: PointOnObject(g3,g6)
    c: PointOnObject(g4,g6)
    c: PointOnObject(g5,g6)
    c: Coincident(g6,g-1)
    c: PointOnObject(g5,g-2)
    c: DistanceX(g0,g4) = 5.9
    c: Coincident(g4,g7)
    c: PointOnObject(g7,g-4)
    c: Horizontal(g7)
    c: Coincident(g7,g8)
    c: Coincident(g8,g-4)
    c: Coincident(g8,g9)
    c: Coincident(g9,g-3)
    c: Coincident(g9,g10)
    c: PointOnObject(g10,g-3)
    c: Coincident(g10,g11)
    c: Coincident(g11,g0)
    c: Horizontal(g11)
    c: Coincident(g11,g12)
    c: Coincident(g12,g1)
    c: Coincident(g12,g13)
    c: Coincident(g13,g2)
    c: Coincident(g13,g14)
    c: Coincident(g14,g3)
    c: Coincident(g14,g15)
    c: Coincident(g15,g7)
FEATURE [PartDesign::Pocket] Pocket013
  BaseFeature = -> Pad028
  Direction = (0,1,-2e-16)
  Length = 3.7
  Length2 = -0.9
  Placement = pos=(0,0,0) rot=(1,0,0;1.5708rad)
  Profile = -> Sketch047
  ReferenceAxis = -> Sketch047 [N_Axis]
  Type = 4
FEATURE [Sketcher::SketchObject] Sketch048
  ExternalGeometry = -> [Pocket013]
  FullyConstrained = true
  MapMode = 5
  Placement = pos=(0,-4.6,0) rot=(1,0,0;1.5708rad)
  Support = -> [Pocket013]
  sketch-geometry (7):
    g0: LineSegment StartX=-3.75 StartY=-5.2 StartZ=0 EndX=-3.75 EndY=3.2 EndZ=0
    g1: LineSegment StartX=-3.75 StartY=3.2 StartZ=0 EndX=-3.75 EndY=4 EndZ=0
    g2: LineSegment StartX=-3.75 StartY=4 StartZ=0 EndX=-2.2 EndY=6.21363 EndZ=0
    g3: LineSegment StartX=-2.2 StartY=6.21363 StartZ=0 EndX=-2.2 EndY=12.2136 EndZ=0
    g4: LineSegment StartX=-2.2 StartY=12.2136 StartZ=0 EndX=-6.8 EndY=12.2136 EndZ=0
    g5: LineSegment StartX=-6.8 StartY=12.2136 StartZ=0 EndX=-6.8 EndY=-5.2 EndZ=0
    g6: LineSegment StartX=-6.8 StartY=-5.2 StartZ=0 EndX=-3.75 EndY=-5.2 EndZ=0
  constraints (19):
    c: Coincident(g-3,g0)
    c: Coincident(g0,g-3)
    c: Coincident(g0,g1)
    c: Vertical(g1)
    c: Coincident(g1,g2)
    c: Coincident(g2,g3)
    c: Vertical(g3)
    c: Coincident(g3,g4)
    c: Horizontal(g4)
    c: Coincident(g4,g5)
    c: Vertical(g5)
    c: Coincident(g5,g6)
    c: Coincident(g6,g0)
    c: Horizontal(g6)
    c: DistanceX(g6,g6) = 3.05
    c: Angle(g1,g2) = 2.53073
    c: DistanceX(g4,g4) = 4.6
    c: DistanceY(g1,g1) = 0.8
    c: DistanceY(g3,g3) = 6
FEATURE [PartDesign::Pad] Pad029
  BaseFeature = -> Pocket013
  Direction = (0,-1,2e-16)
  Length = 6.15
  Length2 = 1.35
  Placement = pos=(0,0,0) rot=(1,0,0;1.5708rad)
  Profile = -> Sketch048
  ReferenceAxis = -> Sketch048 [N_Axis]
  Type = 4
FEATURE [Sketcher::SketchObject] Sketch049
  ExternalGeometry = -> [Pad029]
  FullyConstrained = true
  MapMode = 5
  Placement = pos=(-6.8,0,0) rot=(0.707107,0,-0.707107;3.14159rad)
  Support = -> [Pad029]
  sketch-geometry (1):
    g0: Circle CenterX=-9.00363 CenterY=7 CenterZ=0 NormalX=0 NormalY=0 NormalZ=1 AngleXU=0 Radius=2
  constraints (3):
    c: Diameter(g0) = 4
    c: DistanceX(g-3,g0) = 3.21
    c: DistanceY(g-3,g0) = 3.75
FEATURE [PartDesign::Pocket] Pocket014
  BaseFeature = -> Pad029
  Direction = (1,0,2e-16)
  Length = 5
  Length2 = 5
  Placement = pos=(0,0,0) rot=(1,0,0;1.5708rad)
  Profile = -> Sketch049
  ReferenceAxis = -> Sketch049 [N_Axis]
  Type = 1
FEATURE [Sketcher::SketchObject] Sketch050
  ExternalGeometry = -> [Pocket014]
  FullyConstrained = true
  MapMode = 5
  Placement = pos=(-6.8,0,0) rot=(0.707107,0,-0.707107;3.14159rad)
  Support = -> [Pocket014]
  sketch-geometry (16):
    g0: LineSegment StartX=-5.59726 StartY=7 StartZ=0 EndX=-7.30045 EndY=9.95 EndZ=0
    g1: LineSegment StartX=-7.30045 StartY=9.95 StartZ=0 EndX=-10.7068 EndY=9.95 EndZ=0
    g2: LineSegment StartX=-10.7068 StartY=9.95 StartZ=0 EndX=-12.41 EndY=7 EndZ=0
    g3: LineSegment StartX=-12.41 StartY=7 StartZ=0 EndX=-10.7068 EndY=4.05 EndZ=0
    g4: LineSegment StartX=-10.7068 StartY=4.05 StartZ=0 EndX=-7.30045 EndY=4.05 EndZ=0
    g5: LineSegment StartX=-7.30045 StartY=4.05 StartZ=0 EndX=-5.59726 EndY=7 EndZ=0
    g6: Circle CenterX=-9.00363 CenterY=7 CenterZ=0 NormalX=0 NormalY=0 NormalZ=1 AngleXU=0 Radius=3.40637
    g7: LineSegment StartX=-10.7068 StartY=9.95 StartZ=0 EndX=-10.7068 EndY=10.75 EndZ=0
    g8: LineSegment StartX=-10.7068 StartY=10.75 StartZ=0 EndX=-12.2136 EndY=10.75 EndZ=0
    g9: LineSegment StartX=-12.2136 StartY=10.75 StartZ=0 EndX=-12.2136 EndY=3.25 EndZ=0
    g10: LineSegment StartX=-12.2136 StartY=3.25 StartZ=0 EndX=-10.7068 EndY=3.25 EndZ=0
    g11: LineSegment StartX=-10.7068 StartY=3.25 StartZ=0 EndX=-10.7068 EndY=4.05 EndZ=0
    g12: LineSegment StartX=-10.7068 StartY=4.05 StartZ=0 EndX=-7.30045 EndY=4.05 EndZ=0
    g13: LineSegment StartX=-7.30045 StartY=4.05 StartZ=0 EndX=-5.59726 EndY=7 EndZ=0
    g14: LineSegment StartX=-5.59726 StartY=7 StartZ=0 EndX=-7.30045 EndY=9.95 EndZ=0
    g15: LineSegment StartX=-7.30045 StartY=9.95 StartZ=0 EndX=-10.7068 EndY=9.95 EndZ=0
  constraints (36):
    c: Coincident(g0,g1)
    c: Coincident(g1,g2)
    c: Coincident(g2,g3)
    c: Coincident(g3,g4)
    c: Coincident(g4,g5)
    c: Coincident(g5,g0)
    c: Equal(g0, g1-g5) x5
    c: PointOnObject(g0,g6)
    c: PointOnObject(g1,g6)
    c: PointOnObject(g2,g6)
    c: PointOnObject(g3,g6)
    c: PointOnObject(g4,g6)
    c: PointOnObject(g5,g6)
    c: Horizontal(g1)
    c: DistanceY(g3,g1) = 5.9
    c: Coincident(g1,g7)
    c: Vertical(g7)
    c: Coincident(g7,g8)
    c: Coincident(g8,g9)
    c: Coincident(g9,g10)
    c: Coincident(g10,g11)
    c: Coincident(g11,g3)
    c: Vertical(g11)
    c: Coincident(g11,g12)
    c: Coincident(g12,g4)
    c: Coincident(g12,g13)
    c: Coincident(g13,g0)
    c: Coincident(g13,g14)
    c: Coincident(g14,g0)
    c: Coincident(g14,g15)
    c: Coincident(g15,g7)
    c: PointOnObject(g10,g-3)
    c: PointOnObject(g7,g-4)
    c: Coincident(g9,g-3)
    c: Coincident(g8,g-4)
    c: Coincident(g6,g-5)
FEATURE [PartDesign::Pocket] Pocket015
  BaseFeature = -> Pocket014
  Direction = (1,0,2e-16)
  Length = 3.7
  Length2 = -0.9
  Placement = pos=(0,0,0) rot=(1,0,0;1.5708rad)
  Profile = -> Sketch050
  ReferenceAxis = -> Sketch050 [N_Axis]
  Type = 4
FEATURE [Sketcher::SketchObject] Sketch051
  ExternalGeometry = -> [Pocket015]
  FullyConstrained = true
  MapMode = 5
  Placement = pos=(0,4.1e-15,12.2136) rot=(0,0,1;3.14159rad)
  Support = -> [Pocket015]
  sketch-geometry (4):
    g0: LineSegment StartX=2.2 StartY=3.25 StartZ=0 EndX=3 EndY=3.25 EndZ=0
    g1: LineSegment StartX=3 StartY=3.25 StartZ=0 EndX=3 EndY=3.75 EndZ=0
    g2: LineSegment StartX=3 StartY=3.75 StartZ=0 EndX=2.2 EndY=3.75 EndZ=0
    g3: LineSegment StartX=2.2 StartY=3.75 StartZ=0 EndX=2.2 EndY=3.25 EndZ=0
  constraints (11):
    c: Coincident(g0,g1)
    c: Coincident(g1,g2)
    c: Coincident(g2,g3)
    c: Coincident(g3,g0)
    c: Horizontal(g0)
    c: Horizontal(g2)
    c: Vertical(g1)
    c: Vertical(g3)
    c: Coincident(g0,g-3)
    c: DistanceY(g3,g3) = 0.5
    c: DistanceX(g0,g0) = 0.8
FEATURE [PartDesign::Pocket] Pocket016
  BaseFeature = -> Pocket015
  Direction = (0,-6e-16,-1)
  Length = 8
  Length2 = 5
  Placement = pos=(0,0,0) rot=(1,0,0;1.5708rad)
  Profile = -> Sketch051
  ReferenceAxis = -> Sketch051 [N_Axis]
  Type = 0
FEATURE [PartDesign::Fillet] Fillet008
  Base = -> Pocket016 [Edge30]
  BaseFeature = -> Pocket016
  Placement = pos=(0,0,0) rot=(1,0,0;1.5708rad)
  Radius = 1
  SupportTransform = false
  UseAllEdges = false
FEATURE [PartDesign::Fillet] Fillet009
  Base = -> Fillet008 [Edge30]
  BaseFeature = -> Fillet008
  Placement = pos=(0,0,0) rot=(1,0,0;1.5708rad)
  Radius = 2
  SupportTransform = false
  UseAllEdges = false
FEATURE [PartDesign::Body] Body027  label="3DP_Angle_bracket_Bottom"
  Group = -> [Sketch046,Pad028,Sketch047,Pocket013,Sketch048,Pad029,Sketch049,Pocket014,Sketch050,Pocket015,Sketch051,Pocket016,Fillet008,Fillet009]
  Origin = -> Origin027
  Placement = pos=(-30,36.8,6.9) rot=(0,0,1;0rad)
  Tip = -> Fillet009
FEATURE [App::DocumentObjectGroup] Group007  label="Adapter elements (not needed)"
  Group = -> [Male_Thread__cut_,Body026]
FEATURE [Sketcher::SketchObject] Sketch052
  ExternalGeometry = -> [Fillet007]
  FullyConstrained = true
  MapMode = 5
  Placement = pos=(0,-10.2,2.3e-15) rot=(1,0,0;1.5708rad)
  Support = -> [Fillet007]
  sketch-geometry (4):
    g0: LineSegment StartX=-14.8 StartY=11.74 StartZ=0 EndX=-9.8 EndY=11.74 EndZ=0
    g1: LineSegment StartX=-9.8 StartY=11.74 StartZ=0 EndX=-9.8 EndY=3.24 EndZ=0
    g2: LineSegment StartX=-9.8 StartY=3.24 StartZ=0 EndX=-14.8 EndY=3.24 EndZ=0
    g3: LineSegment StartX=-14.8 StartY=3.24 StartZ=0 EndX=-14.8 EndY=11.74 EndZ=0
  constraints (10):
    c: Coincident(g0,g1)
    c: Coincident(g1,g2)
    c: Coincident(g2,g3)
    c: Coincident(g3,g0)
    c: Horizontal(g0)
    c: Horizontal(g2)
    c: Vertical(g1)
    c: Vertical(g3)
    c: Coincident(g0,g-3)
    c: Coincident(g1,g-4)
FEATURE [PartDesign::Pocket] Pocket017
  BaseFeature = -> Fillet007
  Direction = (0,1,-4e-16)
  Length = 0.2
  Length2 = 5
  Placement = pos=(0,0,0) rot=(1,0,0;1.5708rad)
  Profile = -> Sketch052
  ReferenceAxis = -> Sketch052 [N_Axis]
  Type = 0
FEATURE [Sketcher::SketchObject] Sketch053
  ExternalGeometry = -> [Pocket017]
  FullyConstrained = true
  MapMode = 5
  Placement = pos=(0,-10,6.4e-15) rot=(1,0,0;1.5708rad)
  Support = -> [Pocket017]
  sketch-geometry (4):
    g0: LineSegment StartX=-9.8 StartY=11.74 StartZ=0 EndX=-10.2 EndY=11.74 EndZ=0
    g1: LineSegment StartX=-10.2 StartY=11.74 StartZ=0 EndX=-10.2 EndY=3.24 EndZ=0
    g2: LineSegment StartX=-10.2 StartY=3.24 StartZ=0 EndX=-9.8 EndY=3.24 EndZ=0
    g3: LineSegment StartX=-9.8 StartY=3.24 StartZ=0 EndX=-9.8 EndY=11.74 EndZ=0
  constraints (10):
    c: Coincident(g0,g1)
    c: Coincident(g1,g2)
    c: Coincident(g2,g3)
    c: Coincident(g3,g0)
    c: Horizontal(g0)
    c: Horizontal(g2)
    c: Vertical(g1)
    c: Coincident(g0,g-3)
    c: Coincident(g2,g-3)
    c: DistanceX(g2,g2) = 0.4
FEATURE [PartDesign::Pocket] Pocket018
  BaseFeature = -> Pocket017
  Direction = (0,1,-4e-16)
  Length = 8.7
  Length2 = 5
  Placement = pos=(0,0,0) rot=(1,0,0;1.5708rad)
  Profile = -> Sketch053
  ReferenceAxis = -> Sketch053 [N_Axis]
  Type = 0
FEATURE [Sketcher::SketchObject] Sketch054
  FullyConstrained = true
  MapMode = 5
  Support = -> [XY_Plane029]
  sketch-geometry (4):
    g0: LineSegment StartX=-26.25 StartY=0 StartZ=0 EndX=26.25 EndY=0 EndZ=0
    g1: LineSegment StartX=26.25 StartY=0 StartZ=0 EndX=26.25 EndY=-4 EndZ=0
    g2: LineSegment StartX=26.25 StartY=-4 StartZ=0 EndX=-26.25 EndY=-4 EndZ=0
    g3: LineSegment StartX=-26.25 StartY=-4 StartZ=0 EndX=-26.25 EndY=0 EndZ=0
  constraints (11):
    c: Coincident(g0,g1)
    c: Coincident(g1,g2)
    c: Coincident(g2,g3)
    c: Coincident(g3,g0)
    c: Horizontal(g0)
    c: Vertical(g1)
    c: Vertical(g3)
    c: PointOnObject(g0,g-1)
    c: Symmetric(g2,g1,g-2)
    c: DistanceX(g0,g0) = 52.5
    c: DistanceY(g3,g3) = 4
FEATURE [PartDesign::Pad] Pad030
  Direction = (0,0,1)
  Length = 0.4
  Length2 = 10
  Profile = -> Sketch054
  ReferenceAxis = -> Sketch054 [N_Axis]
  Type = 0
FEATURE [Part::Mirroring] Part__Mirroring  label="3DP_Angle_bracket_Bottom (Mirror #1)"
  Base = (0,0,0)
  Normal = (1,0,0)
  Source = -> Body027
FEATURE [Sketcher::SketchObject] Sketch055
  ExternalGeometry = -> [Pocket018]
  FullyConstrained = true
  MapMode = 5
  Placement = pos=(0,1.7e-15,7.5) rot=(1,0,0;3.14159rad)
  Support = -> [Pocket018]
  sketch-geometry (16):
    g0: LineSegment StartX=-5.5 StartY=4.29363 StartZ=0 EndX=-2.55 EndY=5.99682 EndZ=0
    g1: LineSegment StartX=-2.55 StartY=5.99682 StartZ=0 EndX=-2.55 EndY=9.40318 EndZ=0
    g2: LineSegment StartX=-2.55 StartY=9.40318 StartZ=0 EndX=-5.5 EndY=11.1064 EndZ=0
    g3: LineSegment StartX=-5.5 StartY=11.1064 StartZ=0 EndX=-8.45 EndY=9.40318 EndZ=0
    g4: LineSegment StartX=-8.45 StartY=9.40318 StartZ=0 EndX=-8.45 EndY=5.99682 EndZ=0
    g5: LineSegment StartX=-8.45 StartY=5.99682 StartZ=0 EndX=-5.5 EndY=4.29363 EndZ=0
    g6: Circle CenterX=-5.5 CenterY=7.7 CenterZ=0 NormalX=0 NormalY=0 NormalZ=1 AngleXU=0 Radius=3.40637
    g7: LineSegment StartX=-8.45 StartY=9.40318 StartZ=0 EndX=-8.45 EndY=5.99682 EndZ=0
    g8: LineSegment StartX=-8.45 StartY=5.99682 StartZ=0 EndX=-5.5 EndY=4.29363 EndZ=0
    g9: LineSegment StartX=-5.5 StartY=4.29363 StartZ=0 EndX=-2.55 EndY=5.99682 EndZ=0
    g10: LineSegment StartX=-2.55 StartY=5.99682 StartZ=0 EndX=-2.55 EndY=9.40318 EndZ=0
    g11: LineSegment StartX=-2.55 StartY=9.40318 StartZ=0 EndX=-2 EndY=9.40318 EndZ=0
    g12: LineSegment StartX=-2 StartY=9.40318 StartZ=0 EndX=-2 EndY=1.3 EndZ=0
    g13: LineSegment StartX=-2 StartY=1.3 StartZ=0 EndX=-9 EndY=1.3 EndZ=0
    g14: LineSegment StartX=-9 StartY=1.3 StartZ=0 EndX=-9 EndY=9.40318 EndZ=0
    g15: LineSegment StartX=-9 StartY=9.40318 StartZ=0 EndX=-8.45 EndY=9.40318 EndZ=0
  constraints (36):
    c: Coincident(g0,g1)
    c: Coincident(g1,g2)
    c: Coincident(g2,g3)
    c: Coincident(g3,g4)
    c: Coincident(g4,g5)
    c: Coincident(g5,g0)
    c: Equal(g0, g1-g5) x5
    c: PointOnObject(g0,g6)
    c: PointOnObject(g1,g6)
    c: PointOnObject(g2,g6)
    c: PointOnObject(g3,g6)
    c: PointOnObject(g4,g6)
    c: PointOnObject(g5,g6)
    c: Coincident(g6,g-3)
    c: Vertical(g1)
    c: DistanceX(g3,g1) = 5.9
    c: Coincident(g3,g7)
    c: Coincident(g7,g4)
    c: Coincident(g7,g8)
    c: Coincident(g8,g0)
    c: Coincident(g8,g9)
    c: Coincident(g9,g0)
    c: Coincident(g9,g10)
    c: Coincident(g10,g1)
    c: Coincident(g10,g11)
    c: Horizontal(g11)
    c: Coincident(g11,g12)
    c: Coincident(g12,g-4)
    c: Vertical(g12)
    c: Coincident(g12,g13)
    c: Coincident(g13,g-4)
    c: Coincident(g13,g14)
    c: Vertical(g14)
    c: Coincident(g14,g15)
    c: Coincident(g15,g7)
    c: Horizontal(g15)
FEATURE [PartDesign::Pad] Pad031
  BaseFeature = -> Pocket018
  Direction = (0,-2e-16,-1)
  Length = 2
  Length2 = 10
  Placement = pos=(0,0,0) rot=(1,0,0;1.5708rad)
  Profile = -> Sketch055
  ReferenceAxis = -> Sketch055 [N_Axis]
  Type = 0
FEATURE [PartDesign::Body] Body024  label="3DP_Angle_bracket_Top"
  Group = -> [Sketch037,Pad022,Sketch038,Pad023,Sketch039,Pad024,Sketch040,Pocket010,Sketch041,Pad025,Sketch042,Pocket011,Sketch043,Pocket012,Fillet005,Fillet006,Fillet007,Sketch052,Pocket017,Sketch053,Pocket018,Sketch055,Pad031]
  Origin = -> Origin024
  Placement = pos=(-21.5,36.8,85) rot=(0,0,1;0rad)
  Tip = -> Pad031
FEATURE [Part::Mirroring] Part__Mirroring001  label="3DP_Angle_bracket_Top (Mirror #2)"
  Base = (0,0,0)
  Normal = (1,0,0)
  Source = -> Body024
FEATURE [Sketcher::SketchObject] Sketch056
  FullyConstrained = true
  MapMode = 5
  Placement = pos=(0,0,0) rot=(1,0,0;1.5708rad)
  Support = -> [XZ_Plane030]
  sketch-geometry (4):
    g0: LineSegment StartX=-17 StartY=0 StartZ=0 EndX=17 EndY=0 EndZ=0
    g1: LineSegment StartX=17 StartY=0 StartZ=0 EndX=17 EndY=-4 EndZ=0
    g2: LineSegment StartX=17 StartY=-4 StartZ=0 EndX=-17 EndY=-4 EndZ=0
    g3: LineSegment StartX=-17 StartY=-4 StartZ=0 EndX=-17 EndY=0 EndZ=0
  constraints (11):
    c: Coincident(g0,g1)
    c: Coincident(g1,g2)
    c: Coincident(g2,g3)
    c: Coincident(g3,g0)
    c: Horizontal(g0)
    c: Vertical(g1)
    c: Vertical(g3)
    c: PointOnObject(g0,g-1)
    c: Symmetric(g1,g2,g-2)
    c: DistanceX(g0,g0) = 34
    c: DistanceY(g3,g3) = 4
FEATURE [PartDesign::Pad] Pad032
  Direction = (0,-1,2e-16)
  Length = 0.4
  Length2 = 10
  Placement = pos=(0,0,0) rot=(1,0,0;1.5708rad)
  Profile = -> Sketch056
  ReferenceAxis = -> Sketch056 [N_Axis]
  Type = 0
FEATURE [Sketcher::SketchObject] Sketch057
  FullyConstrained = true
  MapMode = 5
  Support = -> [XY_Plane031]
  sketch-geometry (8):
    g0: LineSegment StartX=4.1 StartY=0 StartZ=0 EndX=2.05 EndY=3.5507 EndZ=0
    g1: LineSegment StartX=2.05 StartY=3.5507 StartZ=0 EndX=-2.05 EndY=3.5507 EndZ=0
    g2: LineSegment StartX=-2.05 StartY=3.5507 StartZ=0 EndX=-4.1 EndY=2.2e-15 EndZ=0
    g3: LineSegment StartX=-4.1 StartY=2.2e-15 StartZ=0 EndX=-2.05 EndY=-3.5507 EndZ=0
    g4: LineSegment StartX=-2.05 StartY=-3.5507 StartZ=0 EndX=2.05 EndY=-3.5507 EndZ=0
    g5: LineSegment StartX=2.05 StartY=-3.5507 StartZ=0 EndX=4.1 EndY=0 EndZ=0
    g6: Circle CenterX=0 CenterY=0 CenterZ=0 NormalX=0 NormalY=0 NormalZ=1 AngleXU=0 Radius=4.1
    g7: Circle CenterX=0 CenterY=0 CenterZ=0 NormalX=0 NormalY=0 NormalZ=1 AngleXU=0 Radius=1.8
  constraints (18):
    c: Coincident(g0,g1)
    c: Coincident(g1,g2)
    c: Coincident(g2,g3)
    c: Coincident(g3,g4)
    c: Coincident(g4,g5)
    c: Coincident(g5,g0)
    c: Equal(g0, g1-g5) x5
    c: PointOnObject(g0,g6)
    c: PointOnObject(g1,g6)
    c: PointOnObject(g2,g6)
    c: PointOnObject(g3,g6)
    c: PointOnObject(g4,g6)
    c: PointOnObject(g5,g6)
    c: Coincident(g6,g-1)
    c: PointOnObject(g5,g-1)
    c: Distance(g4) = 4.1
    c: Coincident(g7,g6)
    c: Diameter(g7) = 3.6
FEATURE [PartDesign::Pad] Pad036
  AlongSketchNormal = false
  Direction = (0,0,1)
  Length = 1
  Length2 = 100
  Profile = -> Sketch057
  Type = 0
FEATURE [Sketcher::SketchObject] Sketch058
  ExternalGeometry = -> [Pad036]
  FullyConstrained = true
  MapMode = 5
  Placement = pos=(0,0,1) rot=(0,0,1;0rad)
  Support = -> [Pad036]
  sketch-geometry (14):
    g0: LineSegment StartX=4.1 StartY=0 StartZ=0 EndX=2.05 EndY=3.5507 EndZ=0
    g1: LineSegment StartX=2.05 StartY=3.5507 StartZ=0 EndX=-2.05 EndY=3.5507 EndZ=0
    g2: LineSegment StartX=-2.05 StartY=3.5507 StartZ=0 EndX=-4.1 EndY=0 EndZ=0
    g3: LineSegment StartX=-4.1 StartY=1e-16 StartZ=0 EndX=-2.05 EndY=-3.5507 EndZ=0
    g4: LineSegment StartX=-2.05 StartY=-3.5507 StartZ=0 EndX=2.05 EndY=-3.5507 EndZ=0
    g5: LineSegment StartX=2.05 StartY=-3.5507 StartZ=0 EndX=4.1 EndY=0 EndZ=0
    g6: Circle CenterX=0 CenterY=0 CenterZ=0 NormalX=0 NormalY=0 NormalZ=1 AngleXU=0 Radius=4.1
    g7: LineSegment StartX=3.2909 StartY=0 StartZ=0 EndX=1.64545 EndY=2.85 EndZ=0
    g8: LineSegment StartX=1.64545 StartY=2.85 StartZ=0 EndX=-1.64545 EndY=2.85 EndZ=0
    g9: LineSegment StartX=-1.64545 StartY=2.85 StartZ=0 EndX=-3.2909 EndY=0 EndZ=0
    g10: LineSegment StartX=-3.2909 StartY=0 StartZ=0 EndX=-1.64545 EndY=-2.85 EndZ=0
    g11: LineSegment StartX=-1.64545 StartY=-2.85 StartZ=0 EndX=1.64545 EndY=-2.85 EndZ=0
    g12: LineSegment StartX=1.64545 StartY=-2.85 StartZ=0 EndX=3.2909 EndY=0 EndZ=0
    g13: Circle CenterX=0 CenterY=0 CenterZ=0 NormalX=0 NormalY=0 NormalZ=1 AngleXU=0 Radius=3.2909
  constraints (31):
    c: Coincident(g0,g1)
    c: Coincident(g1,g2)
    c: Coincident(g2,g3)
    c: Coincident(g3,g4)
    c: Coincident(g4,g5)
    c: Coincident(g5,g0)
    c: Equal(g0, g1-g5) x5
    c: PointOnObject(g0,g6)
    c: PointOnObject(g1,g6)
    c: PointOnObject(g2,g6)
    c: PointOnObject(g3,g6)
    c: PointOnObject(g4,g6)
    c: PointOnObject(g5,g6)
    c: Coincident(g6,g-1)
    c: Coincident(g5,g-3)
    c: Coincident(g7,g8)
    c: Coincident(g8,g9)
    c: Coincident(g9,g10)
    c: Coincident(g10,g11)
    c: Coincident(g11,g12)
    c: Coincident(g12,g7)
    c: Equal(g7, g8-g12) x5
    c: PointOnObject(g7,g13)
    c: PointOnObject(g8,g13)
    c: PointOnObject(g9,g13)
    c: PointOnObject(g10,g13)
    c: PointOnObject(g11,g13)
    c: PointOnObject(g12,g13)
    c: Coincident(g13,g6)
    c: PointOnObject(g12,g-1)
    c: Distance(g7,g11) = 5.7
FEATURE [PartDesign::Pad] Pad037
  AlongSketchNormal = false
  BaseFeature = -> Pad036
  Direction = (0,0,1)
  Length = 2
  Length2 = 100
  Profile = -> Sketch058
  Type = 0
FEATURE [Sketcher::SketchObject] Sketch059
  ExternalGeometry = -> [Pad037]
  FullyConstrained = true
  MapMode = 5
  Placement = pos=(0,0,0) rot=(0.57735,0.57735,0.57735;2.0944rad)
  Support = -> [YZ_Plane031]
  sketch-geometry (5):
    g0: LineSegment StartX=-3.5507 StartY=-1.6e-15 StartZ=0 EndX=-3.5507 EndY=2.6 EndZ=0
    g1: LineSegment StartX=-3.5507 StartY=2.6 StartZ=0 EndX=-5.65247 EndY=1.61993 EndZ=0
    g2: LineSegment StartX=-5.65247 StartY=1.61993 StartZ=0 EndX=-11.5507 EndY=1 EndZ=0
    g3: LineSegment StartX=-11.5507 StartY=1 StartZ=0 EndX=-11.5507 EndY=0 EndZ=0
    g4: LineSegment StartX=-11.5507 StartY=0 StartZ=0 EndX=-3.5507 EndY=-1.6e-15 EndZ=0
  constraints (14):
    c: Coincident(g-3,g0)
    c: PointOnObject(g0,g-4)
    c: Coincident(g0,g1)
    c: Coincident(g1,g2)
    c: Coincident(g2,g3)
    c: PointOnObject(g3,g-1)
    c: Vertical(g3)
    c: Coincident(g3,g4)
    c: Coincident(g4,g0)
    c: Distance(g4) = 8
    c: Distance(g3) = 1
    c: Distance(g0) = 2.6
    c: Angle(g3,g2) = 1.67552
    c: Angle(g1,g0) = 1.13446
FEATURE [PartDesign::Pad] Pad038
  AlongSketchNormal = false
  BaseFeature = -> Pad037
  Direction = (1,-2e-16,3e-16)
  Length = 2
  Length2 = 100
  Midplane = true
  Profile = -> Sketch059
  ReferenceAxis = -> Sketch059 [N_Axis]
  Type = 0
FEATURE [PartDesign::Fillet] Fillet010
  Base = -> Pad038 [Edge70]
  BaseFeature = -> Pad038
  Radius = 9
  SupportTransform = false
  UseAllEdges = false
FEATURE [PartDesign::PolarPattern] PolarPattern001
  Angle = 360
  Axis = -> Z_Axis031
  BaseFeature = -> Fillet010
  Occurrences = 3
  Originals = -> [Pad038,Fillet010]
FEATURE [PartDesign::Body] Body031  label="3DP_Wrench"
  Group = -> [Sketch057,Pad036,Sketch058,Pad037,Sketch059,Pad038,Fillet010,PolarPattern001]
  Origin = -> Origin031
  Placement = pos=(70,0,0) rot=(0,0,1;0rad)
  Tip = -> PolarPattern001
FEATURE [Sketcher::SketchObject] Sketch060
  FullyConstrained = true
  MapMode = 5
  Support = -> [XY_Plane032]
  sketch-geometry (7):
    g0: Circle CenterX=0 CenterY=0 CenterZ=0 NormalX=0 NormalY=0 NormalZ=1 AngleXU=0 Radius=33.75
    g1: Circle CenterX=0 CenterY=-22.5 CenterZ=0 NormalX=0 NormalY=0 NormalZ=1 AngleXU=0 Radius=8.5
    g2: Circle CenterX=0 CenterY=-22.5 CenterZ=0 NormalX=0 NormalY=0 NormalZ=1 AngleXU=0 Radius=1
    g3: LineSegment StartX=-2.5 StartY=-28.9 StartZ=0 EndX=-2.5 EndY=-19.9 EndZ=0
    g4: LineSegment StartX=-2.5 StartY=-19.9 StartZ=0 EndX=2.5 EndY=-19.9 EndZ=0
    g5: LineSegment StartX=2.5 StartY=-19.9 StartZ=0 EndX=2.5 EndY=-28.9 EndZ=0
    g6: ArcOfCircle CenterX=0 CenterY=0 CenterZ=0 NormalX=0 NormalY=0 NormalZ=1 AngleXU=0 Radius=29.0079 StartAngle=4.79868 EndAngle=10.9093
  constraints (18):
    c: Coincident(g0,g-1)
    c: Diameter(g0) = 67.5
    c: PointOnObject(g1,g-2)
    c: Diameter(g1) = 17
    c: DistanceY(g1,g-1) = 22.5
    c: Coincident(g2,g1)
    c: Diameter(g2) = 2
    c: Vertical(g3)
    c: Coincident(g3,g4)
    c: Coincident(g4,g5)
    c: Vertical(g5)
    c: Symmetric(g3,g4,g-2)
    c: DistanceX(g4,g4) = 5
    c: DistanceY(g5,g-1) = 28.9
    c: DistanceY(g5,g5) = 9
    c: Coincident(g6,g0)
    c: Coincident(g6,g3)
    c: Coincident(g6,g5)
FEATURE [PartDesign::Pad] Pad039
  Direction = (0,0,1)
  Length = 0.4
  Length2 = 10
  Profile = -> Sketch060
  ReferenceAxis = -> Sketch060 [N_Axis]
  Type = 0
FEATURE [PartDesign::Body] Body032  label="3DP_Drilling_template"
  Group = -> [Sketch060,Pad039]
  Origin = -> Origin032
  Placement = pos=(0,0,83.25) rot=(0,0,1;0rad)
  Tip = -> Pad039
FEATURE [Sketcher::SketchObject] Sketch061
  FullyConstrained = true
  MapMode = 5
  Placement = pos=(0,0,0.4) rot=(0,0,1;0rad)
  Support = -> [Pad030]
  sketch-geometry (3):
    g0: LineSegment StartX=0 StartY=-0.5 StartZ=0 EndX=-1.73205 EndY=-3.5 EndZ=0
    g1: LineSegment StartX=-1.73205 StartY=-3.5 StartZ=0 EndX=1.73205 EndY=-3.5 EndZ=0
    g2: LineSegment StartX=1.73205 StartY=-3.5 StartZ=0 EndX=0 EndY=-0.5 EndZ=0
  constraints (8):
    c: PointOnObject(g0,g-2)
    c: Coincident(g0,g1)
    c: Coincident(g1,g2)
    c: Coincident(g2,g0)
    c: Symmetric(g0,g1,g-2)
    c: DistanceY(g1,g0) = 3
    c: DistanceY(g0,g-1) = 0.5
    c: Equal(g1,g2)
FEATURE [PartDesign::Pad] Pad040
  BaseFeature = -> Pad030
  Direction = (0,0,1)
  Length = 0.2
  Length2 = 10
  Profile = -> Sketch061
  ReferenceAxis = -> Sketch061 [N_Axis]
  Type = 0
FEATURE [PartDesign::Body] Body029  label="Connector_bottom"
  Group = -> [Sketch054,Pad030,Sketch061,Pad040]
  Origin = -> Origin029
  Placement = pos=(0,36.2,1.7) rot=(0,0,1;0rad)
  Tip = -> Pad040
FEATURE [Sketcher::SketchObject] Sketch062
  FullyConstrained = true
  MapMode = 5
  Placement = pos=(0,-0.4,2e-16) rot=(1,0,0;1.5708rad)
  Support = -> [Pad032]
  sketch-geometry (3):
    g0: LineSegment StartX=0 StartY=-0.5 StartZ=0 EndX=-1.73205 EndY=-3.5 EndZ=0
    g1: LineSegment StartX=-1.73205 StartY=-3.5 StartZ=0 EndX=1.73205 EndY=-3.5 EndZ=0
    g2: LineSegment StartX=1.73205 StartY=-3.5 StartZ=0 EndX=0 EndY=-0.5 EndZ=0
  constraints (8):
    c: PointOnObject(g0,g-2)
    c: Coincident(g0,g1)
    c: Coincident(g1,g2)
    c: Coincident(g2,g0)
    c: Symmetric(g0,g1,g-2)
    c: DistanceY(g1,g0) = 3
    c: DistanceY(g0,g-1) = 0.5
    c: Equal(g1,g2)
FEATURE [PartDesign::Pad] Pad041
  BaseFeature = -> Pad032
  Direction = (0,-1,4e-16)
  Length = 0.2
  Length2 = 10
  Placement = pos=(0,0,0) rot=(1,0,0;1.5708rad)
  Profile = -> Sketch062
  ReferenceAxis = -> Sketch062 [N_Axis]
  Type = 0
FEATURE [PartDesign::Body] Body030  label="Connector_top"
  Group = -> [Sketch056,Pad032,Sketch062,Pad041]
  Origin = -> Origin030
  Placement = pos=(0,36.8,87.65) rot=(0,0,1;0rad)
  Tip = -> Pad041
FEATURE [Sketcher::SketchObject] Sketch
  FullyConstrained = true
  MapMode = 5
  Placement = pos=(0,0,0) rot=(1,0,0;1.5708rad)
  Support = -> [XZ_Plane]
  sketch-geometry (19):
    g0: LineSegment StartX=-16 StartY=0 StartZ=0 EndX=-16 EndY=16 EndZ=0
    g1: LineSegment StartX=-16 StartY=16 StartZ=0 EndX=-12 EndY=16 EndZ=0
    g2: LineSegment StartX=-12 StartY=16 StartZ=0 EndX=-12 EndY=21 EndZ=0
    g3: LineSegment StartX=-12 StartY=21 StartZ=0 EndX=-7 EndY=21 EndZ=0
    g4: LineSegment StartX=-7 StartY=21 StartZ=0 EndX=-7 EndY=32 EndZ=0
    g5: LineSegment StartX=-7 StartY=32 StartZ=0 EndX=-11.5 EndY=32 EndZ=0
    g6: LineSegment StartX=-11.5 StartY=32 StartZ=0 EndX=-11.5 EndY=57.5 EndZ=0
    g7: LineSegment StartX=-11.5 StartY=57.5 StartZ=0 EndX=0 EndY=57.5 EndZ=0
    g8: LineSegment StartX=0 StartY=57.5 StartZ=0 EndX=0 EndY=-32 EndZ=0
    g9: LineSegment StartX=0 StartY=-32 StartZ=0 EndX=-3.5 EndY=-32 EndZ=0
    g10: LineSegment StartX=-3.5 StartY=-32 StartZ=0 EndX=-3.5 EndY=-18 EndZ=0
    g11: LineSegment StartX=-3.5 StartY=-18 StartZ=0 EndX=-4.5 EndY=-18 EndZ=0
    g12: LineSegment StartX=-4.5 StartY=-18 StartZ=0 EndX=-4.5 EndY=-12 EndZ=0
    g13: LineSegment StartX=-4.5 StartY=-12 StartZ=0 EndX=-6 EndY=-12 EndZ=0
    g14: LineSegment StartX=-6 StartY=-12 StartZ=0 EndX=-6 EndY=0 EndZ=0
    g15: LineSegment StartX=-6 StartY=0 StartZ=0 EndX=-6 EndY=10 EndZ=0
    g16: LineSegment StartX=-6 StartY=10 StartZ=0 EndX=-13 EndY=10 EndZ=0
    g17: LineSegment StartX=-13 StartY=10 StartZ=0 EndX=-13 EndY=0 EndZ=0
    g18: LineSegment StartX=-13 StartY=0 StartZ=0 EndX=-16 EndY=0 EndZ=0
  constraints (57):
    c: Vertical(g0)
    c: Coincident(g0,g1)
    c: Horizontal(g1)
    c: Coincident(g1,g2)
    c: Vertical(g2)
    c: Coincident(g2,g3)
    c: Horizontal(g3)
    c: Coincident(g3,g4)
    c: Vertical(g4)
    c: Coincident(g4,g5)
    c: Horizontal(g5)
    c: Coincident(g5,g6)
    c: Vertical(g6)
    c: Coincident(g6,g7)
    c: PointOnObject(g7,g-2)
    c: Horizontal(g7)
    c: Coincident(g7,g8)
    c: PointOnObject(g8,g-2)
    c: Coincident(g8,g9)
    c: Horizontal(g9)
    c: Coincident(g9,g10)
    c: Vertical(g10)
    c: Coincident(g10,g11)
    c: Horizontal(g11)
    c: Coincident(g11,g12)
    c: Vertical(g12)
    c: Coincident(g12,g13)
    c: Horizontal(g13)
    c: Coincident(g13,g14)
    c: Vertical(g14)
    c: PointOnObject(g14,g-1)
    c: Coincident(g14,g15)
    c: Vertical(g15)
    c: Coincident(g15,g16)
    c: Horizontal(g16)
    c: Coincident(g16,g17)
    c: PointOnObject(g17,g-1)
    c: Vertical(g17)
    c: Coincident(g17,g18)
    c: Coincident(g18,g0)
    c: Horizontal(g18)
    c: DistanceX(g7,g7) = 11.5
    c: DistanceY(g6,g6) = 25.5
    c: DistanceX(g4,g-1) = 7
    c: DistanceY(g4,g4) = 11
    c: DistanceX(g2,g-1) = 12
    c: DistanceY(g2,g2) = 5
    c: DistanceX(g0,g-1) = 16
    c: DistanceY(g0,g0) = 16
    c: DistanceX(g18,g18) = 3
    c: DistanceX(g15,g-1) = 6
    c: DistanceY(g15,g15) = 10
    c: DistanceY(g14,g14) = 12
    c: DistanceX(g12,g-1) = 4.5
    c: DistanceY(g12,g12) = 6
    c: DistanceX(g10,g-1) = 3.5
    c: DistanceY(g10,g10) = 14
FEATURE [PartDesign::Revolution] Revolution
  Angle = 360
  Axis = (0,-2e-16,1)
  Base = (0,0,0)
  Placement = pos=(0,0,0) rot=(1,0,0;1.5708rad)
  Profile = -> Sketch
  ReferenceAxis = -> Sketch [V_Axis]
FEATURE [Sketcher::SketchObject] Sketch063
  FullyConstrained = true
  MapMode = 5
  Placement = pos=(0,0,0) rot=(1,0,0;1.5708rad)
  Support = -> [XZ_Plane]
  sketch-geometry (2):
    g0: Circle CenterX=0 CenterY=51 CenterZ=0 NormalX=0 NormalY=0 NormalZ=1 AngleXU=0 Radius=2.5
    g1: Circle CenterX=0 CenterY=51 CenterZ=0 NormalX=0 NormalY=0 NormalZ=1 AngleXU=0 Radius=1.8
  constraints (5):
    c: PointOnObject(g0,g-2)
    c: Diameter(g0) = 5
    c: Coincident(g1,g0)
    c: Diameter(g1) = 3.6
    c: DistanceY(g-1,g0) = 51
FEATURE [Sketcher::SketchObject] Sketch064
  FullyConstrained = false
  MapMode = 5
  Placement = pos=(0,0,0) rot=(0.57735,0.57735,0.57735;2.0944rad)
  Support = -> [YZ_Plane]
  sketch-geometry (14):
    g0: LineSegment StartX=0 StartY=51 StartZ=0 EndX=-11.5 EndY=51 EndZ=0
    g1: LineSegment StartX=-11.5 StartY=51 StartZ=0 EndX=-31.5 EndY=51 EndZ=0
    g2: LineSegment StartX=-31.5 StartY=51 StartZ=0 EndX=-45 EndY=48.6196 EndZ=0
    g3-g8: Circle x6 (B-spline internal-alignment scaffolding for g9; pole/knot coordinates omitted)
    g9: BSplineCurve PolesCount=6 KnotsCount=4 Degree=3 IsPeriodic=0
    g10-g13: GeomPoint x4 (B-spline internal-alignment scaffolding for g9; pole/knot coordinates omitted)
  constraints (18):
    c: PointOnObject(g0,g-2)
    c: Horizontal(g0)
    c: Coincident(g0,g1)
    c: Horizontal(g1)
    c: Coincident(g1,g2)
    c: DistanceY(g-1,g0) = 51
    c: DistanceX(g0,g0) = 11.5
    c: DistanceX(g1,g1) = 20
    c: DistanceX(g2,g-1) = 45
    c: Angle(g2,g1) = 2.96706
    c: Weight(g3) = 1
    c: Coincident(g9,g0)
    c: Equal(g3,g4)
    c: Coincident(g4,g0)
    c: Equal(g3, g5-g8) x4
    c: Coincident(g9,g2)
    c: InternalAlignment(g3-g8 -> g9) x6
    c: InternalAlignment(g10-g13 -> g9) x4
FEATURE [PartDesign::AdditivePipe] AdditivePipe
  AuxilleryCurvelinear = true
  AuxillerySpineTangent = false
  BaseFeature = -> Revolution
  Binormal = (0,0,0)
  Mode = 0
  Placement = pos=(0,0,0) rot=(1,0,0;1.5708rad)
  Profile = -> Sketch063
  Spine = -> Sketch064
  SpineTangent = false
  Transformation = 0
  Transition = 0
FEATURE [PartDesign::Fillet] Fillet
  Base = -> AdditivePipe [Edge2,Edge5,Edge8,Edge11]
  BaseFeature = -> AdditivePipe
  Placement = pos=(0,0,0) rot=(1,0,0;1.5708rad)
  Radius = 1
  SupportTransform = false
  UseAllEdges = false
FEATURE [PartDesign::Fillet] Fillet011
  Base = -> Fillet [Edge34]
  BaseFeature = -> Fillet
  Placement = pos=(0,0,0) rot=(1,0,0;1.5708rad)
  Radius = 1.5
  SupportTransform = false
  UseAllEdges = false
FEATURE [PartDesign::Chamfer] Chamfer
  Angle = 45
  Base = -> Fillet011 [Edge37]
  BaseFeature = -> Fillet011
  ChamferType = 0
  FlipDirection = false
  Placement = pos=(0,0,0) rot=(1,0,0;1.5708rad)
  Size = 1
  Size2 = 1
  SupportTransform = false
  UseAllEdges = false
FEATURE [Sketcher::SketchObject] Sketch065
  FullyConstrained = true
  MapMode = 5
  Placement = pos=(0,-7.1e-15,-32) rot=(1,0,0;3.14159rad)
  Support = -> [Chamfer]
  sketch-geometry (1):
    g0: Circle CenterX=0 CenterY=0 CenterZ=0 NormalX=0 NormalY=0 NormalZ=1 AngleXU=0 Radius=2.5
  constraints (2):
    c: Coincident(g0,g-1)
    c: Diameter(g0) = 5
FEATURE [PartDesign::Pocket] Pocket019
  BaseFeature = -> Chamfer
  Direction = (0,-2e-16,1)
  Length = 40
  Length2 = 5
  Placement = pos=(0,0,0) rot=(1,0,0;1.5708rad)
  Profile = -> Sketch065
  ReferenceAxis = -> Sketch065 [N_Axis]
  Type = 0
FEATURE [PartDesign::Body] Body  label="Pump"
  Group = -> [Sketch,Revolution,Sketch063,Sketch064,AdditivePipe,Fillet,Fillet011,Chamfer,Sketch065,Pocket019]
  Origin = -> Origin
  Placement = pos=(0,-22.5,106.5) rot=(0,0,1;0rad)
  Tip = -> Pocket019
FEATURE [Sketcher::SketchObject] Sketch066
  FullyConstrained = true
  MapMode = 5
  Support = -> [XY_Plane033]
  sketch-geometry (2):
    g0: Circle CenterX=0 CenterY=0 CenterZ=0 NormalX=0 NormalY=0 NormalZ=1 AngleXU=0 Radius=2
    g1: Circle CenterX=0 CenterY=0 CenterZ=0 NormalX=0 NormalY=0 NormalZ=1 AngleXU=0 Radius=2.5
  constraints (4):
    c: Coincident(g0,g-1)
    c: Coincident(g1,g0)
    c: Diameter(g0) = 4
    c: Diameter(g1) = 5
FEATURE [PartDesign::Pad] Pad
  Direction = (0,0,1)
  Length = 109
  Length2 = 10
  Profile = -> Sketch066
  ReferenceAxis = -> Sketch066 [N_Axis]
  Type = 0
FEATURE [Sketcher::SketchObject] Sketch067
  FullyConstrained = true
  MapMode = 5
  Placement = pos=(0,0,0) rot=(1,0,0;1.5708rad)
  Support = -> [XZ_Plane033]
  sketch-geometry (3):
    g0: LineSegment StartX=5 StartY=0 StartZ=0 EndX=-5 EndY=10 EndZ=0
    g1: LineSegment StartX=-5 StartY=10 StartZ=0 EndX=-5 EndY=0 EndZ=0
    g2: LineSegment StartX=-5 StartY=0 StartZ=0 EndX=5 EndY=0 EndZ=0
  constraints (8):
    c: PointOnObject(g0,g-1)
    c: Coincident(g0,g1)
    c: Vertical(g1)
    c: Coincident(g1,g2)
    c: Coincident(g2,g0)
    c: Angle(g0,g2) = 0.785398
    c: Symmetric(g1,g0,g-2)
    c: DistanceX(g2,g2) = 10
FEATURE [PartDesign::Pocket] Pocket020
  BaseFeature = -> Pad
  Direction = (0,1,2e-16)
  Length = 5
  Length2 = 5
  Midplane = true
  Profile = -> Sketch067
  ReferenceAxis = -> Sketch067 [N_Axis]
  Type = 0
FEATURE [PartDesign::Body] Body033  label="Pipe"
  Group = -> [Sketch066,Pad,Sketch067,Pocket020]
  Origin = -> Origin033
  Placement = pos=(0,-22.5,5) rot=(0,0,1;0rad)
  Tip = -> Pocket020
FEATURE [App::DocumentObjectGroup] Group  label="Pump + Pipe"
  Group = -> [Body,Body033]
FEATURE [Sketcher::SketchObject] Sketch068
  FullyConstrained = true
  MapMode = 5
  Placement = pos=(0,0,0) rot=(1,0,0;1.5708rad)
  Support = -> [XZ_Plane035]
  sketch-geometry (6):
    g0: LineSegment StartX=-35 StartY=0 StartZ=0 EndX=-35 EndY=11 EndZ=0
    g1: LineSegment StartX=-35 StartY=11 StartZ=0 EndX=0 EndY=11 EndZ=0
    g2: LineSegment StartX=0 StartY=11 StartZ=0 EndX=0 EndY=12 EndZ=0
    g3: LineSegment StartX=0 StartY=12 StartZ=0 EndX=-36 EndY=12 EndZ=0
    g4: LineSegment StartX=-36 StartY=12 StartZ=0 EndX=-36 EndY=0 EndZ=0
    g5: LineSegment StartX=-36 StartY=0 StartZ=0 EndX=-35 EndY=0 EndZ=0
  constraints (18):
    c: PointOnObject(g0,g-1)
    c: Vertical(g0)
    c: Coincident(g0,g1)
    c: PointOnObject(g1,g-2)
    c: Horizontal(g1)
    c: Coincident(g1,g2)
    c: PointOnObject(g2,g-2)
    c: Coincident(g2,g3)
    c: Horizontal(g3)
    c: Coincident(g3,g4)
    c: PointOnObject(g4,g-1)
    c: Vertical(g4)
    c: Coincident(g4,g5)
    c: Coincident(g5,g0)
    c: DistanceX(g3,g3) = 36
    c: DistanceX(g5,g5) = 1
    c: DistanceY(g2,g2) = 1
    c: DistanceY(g4,g4) = 12
FEATURE [PartDesign::Revolution] Revolution005
  Angle = 360
  Axis = (0,-2e-16,1)
  Base = (0,0,0)
  Placement = pos=(0,0,0) rot=(1,0,0;1.5708rad)
  Profile = -> Sketch068
  ReferenceAxis = -> Sketch068 [V_Axis]
FEATURE [Sketcher::SketchObject] Sketch069
  FullyConstrained = true
  MapMode = 5
  Placement = pos=(0,2.7e-15,12) rot=(0,0,1;3.14159rad)
  Support = -> [Revolution005]
  sketch-geometry (1):
    g0: Circle CenterX=0 CenterY=22.5 CenterZ=0 NormalX=0 NormalY=0 NormalZ=1 AngleXU=0 Radius=4
  constraints (3):
    c: PointOnObject(g0,g-2)
    c: Diameter(g0) = 8
    c: DistanceY(g-1,g0) = 22.5
FEATURE [PartDesign::Pocket] Pocket021
  BaseFeature = -> Revolution005
  Direction = (0,2e-16,-1)
  Length = 5
  Length2 = 5
  Placement = pos=(0,0,0) rot=(1,0,0;1.5708rad)
  Profile = -> Sketch069
  ReferenceAxis = -> Sketch069 [N_Axis]
  Type = 1
FEATURE [PartDesign::Body] Body035  label="Jar_Lid"
  Group = -> [Sketch068,Revolution005,Sketch069,Pocket021]
  Origin = -> Origin035
  Placement = pos=(0,0,70) rot=(0,0,1;0rad)
  Tip = -> Pocket021
FEATURE [App::DocumentObjectGroup] Group008  label="Container"
  Group = -> [Body020,Body035,Body004]
FEATURE [Part::FeaturePython] Screw  label="M3x10-Screw"  # Fasteners workbench fastener (typed FeaturePython)
  Placement = pos=(-41.5,29.8,15.9) rot=(0,-1,0;1.5708rad)
  baseObject = -> Body011 [Edge34]
  diameter = 4
  invert = false
  leftHanded = false
  length = 3
  lengthCustom = 10
  matchOuter = true
  offset = 0
  thread = false
  type = 20
FEATURE [Part::FeaturePython] Nut  label="M3-Nut"  # Fasteners workbench fastener (typed FeaturePython)
  Placement = pos=(-33.3,29.8,15.9) rot=(0,-1,0;1.5708rad)
  baseObject = -> Screw [Edge39]
  diameter = 4
  invert = false
  leftHanded = false
  matchOuter = true
  offset = 1.5
  thread = false
  type = 22
FEATURE [Part::FeaturePython] Screw001  label="M3x10-Screw001"  # Fasteners workbench fastener (typed FeaturePython)
  Placement = pos=(-30,41.5,6.9) rot=(-1,0,0;1.5708rad)
  baseObject = -> Body010 [Edge24]
  diameter = 4
  invert = false
  leftHanded = false
  length = 3
  lengthCustom = 10
  matchOuter = true
  offset = 0
  thread = false
  type = 20
FEATURE [Part::FeaturePython] Nut001  label="M3-Nut001"  # Fasteners workbench fastener (typed FeaturePython)
  Placement = pos=(-30,33.3,6.9) rot=(-1,0,0;1.5708rad)
  baseObject = -> Screw001 [Edge39]
  diameter = 4
  invert = false
  leftHanded = false
  matchOuter = true
  offset = 1.5
  thread = false
  type = 22
FEATURE [PartDesign::FeatureBase] Clone007
  BaseFeature = -> Nut001
  Placement = pos=(-30,33.3,6.9) rot=(-0.935113,0.250563,0.250563;1.63783rad)
FEATURE [PartDesign::Body] Body036
  BaseFeature = -> Nut001
  Group = -> [Clone007]
  Origin = -> Origin036
  Tip = -> Clone007
FEATURE [PartDesign::FeatureBase] Clone008
  BaseFeature = -> Nut
  Placement = pos=(-33.3,29.8,26.9) rot=(0,-1,0;1.5708rad)
FEATURE [PartDesign::Body] Body037
  BaseFeature = -> Nut
  Group = -> [Clone008]
  Origin = -> Origin037
  Tip = -> Clone008
FEATURE [PartDesign::FeatureBase] Clone009
  BaseFeature = -> Body036
  Placement = pos=(0,0,16) rot=(0,0,1;0rad)
FEATURE [PartDesign::Body] Body038
  BaseFeature = -> Body036
  Group = -> [Clone009]
  Origin = -> Origin038
  Tip = -> Clone009
FEATURE [Part::FeaturePython] Screw002  label="M3x10-Screw002"  # Fasteners workbench fastener (typed FeaturePython)
  Placement = pos=(-41.5,30.02,92.49) rot=(0,-1,0;1.5708rad)
  baseObject = -> Body011 [Edge35]
  diameter = 4
  invert = false
  leftHanded = false
  length = 3
  lengthCustom = 10
  matchOuter = true
  offset = 0
  thread = false
  type = 20
FEATURE [Part::FeaturePython] Nut002  label="M3-Nut002"  # Fasteners workbench fastener (typed FeaturePython)
  Placement = pos=(-32.8,30.02,92.49) rot=(0,-1,0;1.5708rad)
  baseObject = -> Screw002 [Edge39]
  diameter = 4
  invert = false
  leftHanded = false
  matchOuter = true
  offset = 1
  thread = false
  type = 22
FEATURE [PartDesign::FeatureBase] Clone010
  BaseFeature = -> Nut002
  Placement = pos=(-32.8,30.02,92.49) rot=(-0.250563,-0.935113,0.250563;1.63783rad)
FEATURE [PartDesign::Body] Body039
  BaseFeature = -> Nut002
  Group = -> [Clone010]
  Origin = -> Origin039
  Tip = -> Clone010
FEATURE [Part::FeaturePython] Screw003  label="M3x10-Screw003"  # Fasteners workbench fastener (typed FeaturePython)
  Placement = pos=(-21.5,41.5,85) rot=(-1,0,0;1.5708rad)
  baseObject = -> Body010 [Edge29]
  diameter = 4
  invert = false
  leftHanded = false
  length = 3
  lengthCustom = 10
  matchOuter = true
  offset = 0
  thread = false
  type = 20
FEATURE [Part::FeaturePython] Nut003  label="M3-Nut006"  # Fasteners workbench fastener (typed FeaturePython)
  Placement = pos=(-21.5,33,85) rot=(-1,0,0;1.5708rad)
  baseObject = -> Screw003 [Edge39]
  diameter = 4
  invert = false
  leftHanded = false
  matchOuter = true
  offset = 1.2
  thread = false
  type = 22
FEATURE [PartDesign::FeatureBase] Clone011
  BaseFeature = -> Body039
  Placement = pos=(0,-11,0) rot=(0,0,1;0rad)
FEATURE [PartDesign::Body] Body040
  BaseFeature = -> Body039
  Group = -> [Clone011]
  Origin = -> Origin040
  Tip = -> Clone011
FEATURE [PartDesign::FeatureBase] Clone012
  BaseFeature = -> Nut003
  Placement = pos=(-21.5,23.8,85) rot=(-1,0,0;1.5708rad)
FEATURE [PartDesign::Body] Body041
  BaseFeature = -> Nut003
  Group = -> [Clone012]
  Origin = -> Origin041
  Tip = -> Clone012
FEATURE [Part::FeaturePython] Screw004  label="M3x16-Screw"  # Fasteners workbench fastener (typed FeaturePython)
  Placement = pos=(-27,29.1,92.5) rot=(1,0,0;3.14159rad)
  baseObject = -> Body024 [Edge61]
  diameter = 4
  invert = true
  leftHanded = false
  length = 6
  lengthCustom = 16
  matchOuter = true
  offset = 0
  thread = false
  type = 20
FEATURE [PartDesign::FeatureBase] Clone013
  BaseFeature = -> Screw004
  Placement = pos=(-27,29.1,92.5) rot=(0.965926,0.258819,0;3.14159rad)
FEATURE [PartDesign::Body] Body042
  BaseFeature = -> Screw004
  Group = -> [Clone013]
  Origin = -> Origin042
  Tip = -> Clone013
FEATURE [Part::FeaturePython] Nut004  label="M3-Nut007"  # Fasteners workbench fastener (typed FeaturePython)
  Placement = pos=(-27,29.1,94.6) rot=(0,0,1;0rad)
  baseObject = -> Screw004 [Edge39]
  diameter = 4
  invert = true
  leftHanded = false
  matchOuter = true
  offset = -13.6
  thread = false
  type = 22
FEATURE [PartDesign::FeatureBase] Clone014
  BaseFeature = -> Body042
  Placement = pos=(0,0,-24) rot=(0,0,1;0rad)
FEATURE [PartDesign::Body] Body043
  BaseFeature = -> Body042
  Group = -> [Clone014]
  Origin = -> Origin043
  Tip = -> Clone014
FEATURE [PartDesign::FeatureBase] Clone015
  BaseFeature = -> Nut004
  Placement = pos=(-27,29.1,111.6) rot=(0,0,1;0rad)
FEATURE [PartDesign::Body] Body044
  BaseFeature = -> Nut004
  Group = -> [Clone015]
  Origin = -> Origin044
  Tip = -> Clone015
FEATURE [Part::FeaturePython] Nut005  label="M4-Nut"  # Fasteners workbench fastener (typed FeaturePython)
  Placement = pos=(-27,29.1,103.8) rot=(0,0,1;0rad)
  baseObject = -> Screw004 [Edge39]
  diameter = 1
  invert = true
  leftHanded = false
  matchOuter = true
  offset = -4.4
  thread = false
  type = 11
FEATURE [Part::FeaturePython] Clone016  label="M4-Nut001"  # Draft clone (typed FeaturePython)
  AttacherType = Attacher::AttachEngine3D
  Fuse = false
  Objects = -> [Nut005]
  Placement = pos=(-27,29.08,103.74) rot=(0,0,1;0rad)
  Scale = (0.9,0.9,0.9)
FEATURE [App::DocumentObjectGroup] Group009  label="Offset parts (for build instructions)"
  Group = -> [Body037,Body038,Body040,Body041,Body043,Body044]
FEATURE [App::DocumentObjectGroup] Group010  label="Incorrect angle (not needed, base for clones)"
  Group = -> [Nut001,Nut002,Screw004,Nut005]
FEATURE [Part::FeaturePython] Screw005  label="M3x10-Screw004"  # Fasteners workbench fastener (typed FeaturePython)
  Placement = pos=(-22,-22.5,105.2) rot=(0,0,1;0rad)
  baseObject = -> Body013 [Edge18]
  diameter = 4
  invert = false
  leftHanded = false
  length = 3
  lengthCustom = 10
  matchOuter = true
  offset = 1.5
  thread = false
  type = 20
FEATURE [Part::FeaturePython] Nut006  label="M3-Nut005"  # Fasteners workbench fastener (typed FeaturePython)
  Placement = pos=(-22,-22.5,96.5) rot=(0,0,1;0rad)
  baseObject = -> Screw005 [Edge39]
  diameter = 4
  invert = false
  leftHanded = false
  matchOuter = true
  offset = 1
  thread = false
  type = 22
FEATURE [Mesh::Feature] Angle_bracket_bottom
  Placement = pos=(0,0,0) rot=(0,0,1;3.14159rad)
FEATURE [Mesh::Feature] _lies_on_wrong_side__Angle_bracket_top  label="Angle_bracket_top"
  Placement = pos=(0,0,0) rot=(0,0,1;3.14159rad)
FEATURE [App::DocumentObjectGroup] Group005  label="3D printed parts"
  Group = -> [Body027,Part__Mirroring,Body029,Body024,Part__Mirroring001,Body030,_DP_Adapter_for_pump,Group007,Body031,Body032,Angle_bracket_bottom,_lies_on_wrong_side__Angle_bracket_top]
FEATURE [PartDesign::FeatureBase] Clone017
  BaseFeature = -> Body042
  Placement = pos=(54,0,0) rot=(0,0,1;0rad)
FEATURE [PartDesign::Body] Body045  label="M3_screw_right"
  BaseFeature = -> Body042
  Group = -> [Clone017]
  Origin = -> Origin045
  Tip = -> Clone017
FEATURE [PartDesign::FeatureBase] Clone018
  BaseFeature = -> Nut004
  Placement = pos=(27,29.1,94.6) rot=(0,0,1;0rad)
FEATURE [PartDesign::Body] Body046  label="M3_nut_right"
  BaseFeature = -> Nut004
  Group = -> [Clone018]
  Origin = -> Origin046
  Tip = -> Clone018
FEATURE [PartDesign::FeatureBase] Clone019
  BaseFeature = -> Clone016
  Placement = pos=(27,29.08,103.74) rot=(0,0,1;0rad)
FEATURE [PartDesign::Body] Body047  label="Wingnut_right"
  BaseFeature = -> Clone016
  Group = -> [Clone019]
  Origin = -> Origin047
  Tip = -> Clone019
FEATURE [App::DocumentObjectGroup] Group006  label="Screws and nuts"
  Group = -> [Screw,Nut,Screw001,Body036,Screw002,Body039,Screw003,Nut003,Body042,Nut004,Clone016,Screw005,Nut006,Group009,Group010,Body045,Body046,Body047]
